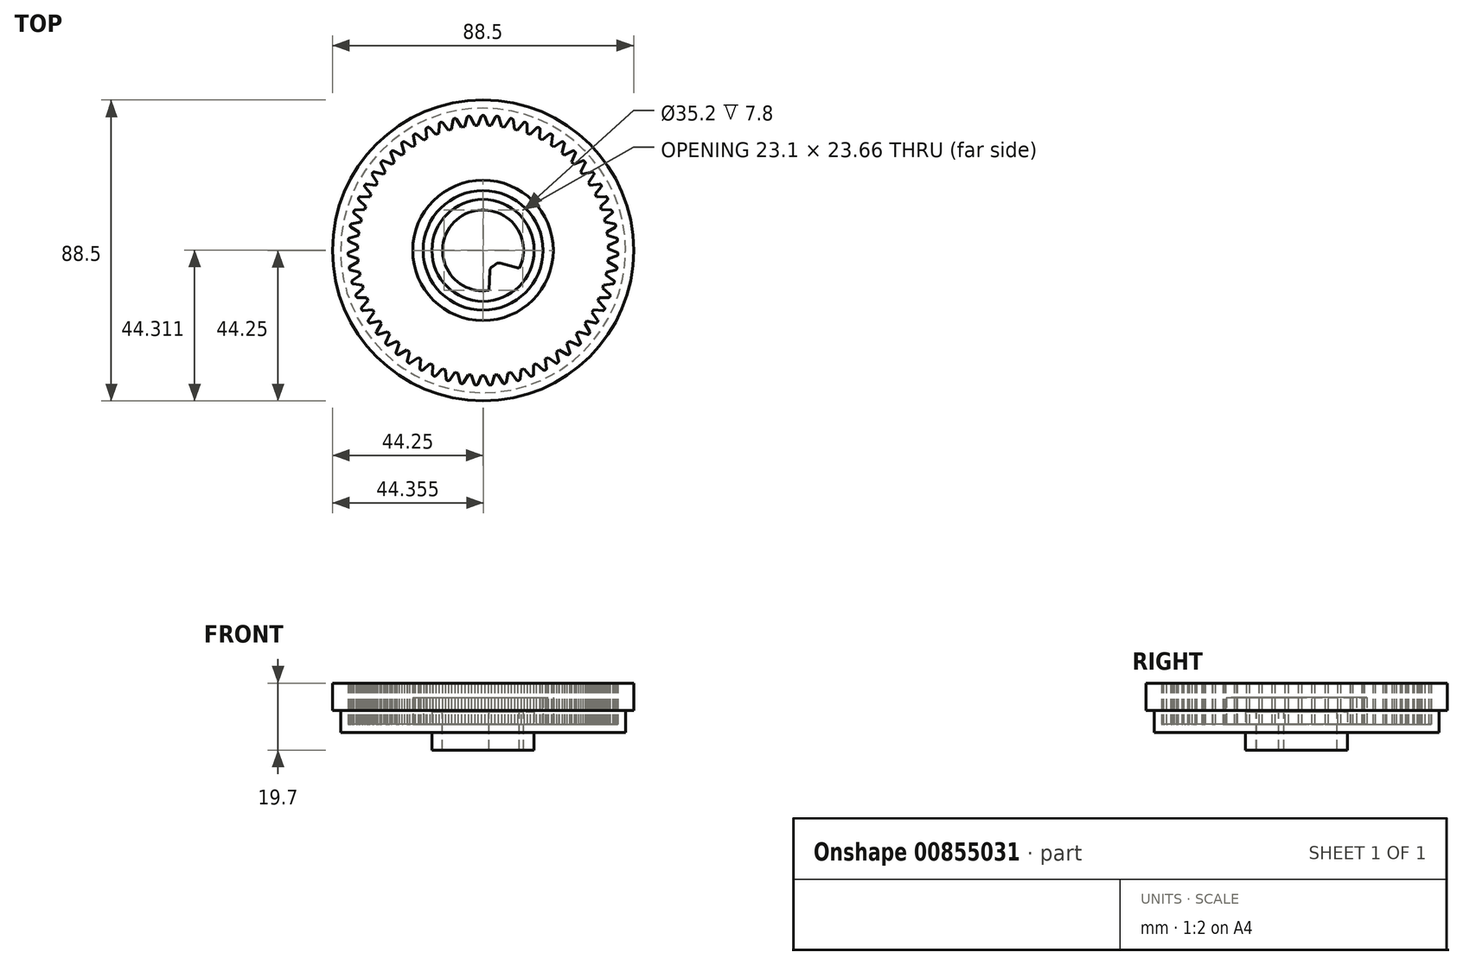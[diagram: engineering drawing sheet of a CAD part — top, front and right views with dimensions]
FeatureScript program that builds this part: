
annotation { "Feature Type Name" : "Feature", "Feature Type Description" : "" }
export const myFeature = defineFeature(function(context is Context, id is Id, definition is map)
    precondition{}
    {
        {
            var Q0;
            Q0=qCreatedBy(makeId("Front.planeOp"),FACE);
            var sketch = newSketch(context, id + "F0", { "sketchPlane" : qUnion([Q0])});
            skLineSegment(sketch, "E0", {"start": v(0, 3.6) * mm, "end": v(-15, 3.6) * mm});
            skLineSegment(sketch, "E1", {"start": v(-15, 3.6) * mm, "end": v(-15, 0) * mm});
            skLineSegment(sketch, "E2", {"start": v(-15, 0) * mm, "end": v(-17.6, 0) * mm});
            skLineSegment(sketch, "E3", {"start": v(-17.6, 0) * mm, "end": v(-17.6, 7.8) * mm});
            skLineSegment(sketch, "E4", {"start": v(-17.6, 7.8) * mm, "end": v(-20.65, 7.8) * mm});
            skLineSegment(sketch, "E5", {"start": v(-20.65, 7.8) * mm, "end": v(-20.65, 0) * mm});
            skLineSegment(sketch, "E6", {"start": v(-20.65, 0) * mm, "end": v(-39.65, 0) * mm});
            skLineSegment(sketch, "E7", {"start": v(-39.65, 0) * mm, "end": v(-39.65, 12.1) * mm});
            skLineSegment(sketch, "E8", {"start": v(-39.65, 12.1) * mm, "end": v(-44.25, 12.1) * mm});
            skLineSegment(sketch, "E9", {"start": v(-44.25, 12.1) * mm, "end": v(-44.25, 4.1) * mm});
            skLineSegment(sketch, "E10", {"start": v(-44.25, 4.1) * mm, "end": v(-41.85, 4.1) * mm});
            skLineSegment(sketch, "E11", {"start": v(-41.85, 4.1) * mm, "end": v(-41.85, -2.4) * mm});
            skLineSegment(sketch, "E12", {"start": v(-41.85, -2.4) * mm, "end": v(-15, -2.4) * mm});
            skLineSegment(sketch, "E13", {"start": v(-15, -2.4) * mm, "end": v(-15, -7.6) * mm});
            skLineSegment(sketch, "E14", {"start": v(-15, -7.6) * mm, "end": v(0, -7.6) * mm});
            skLineSegment(sketch, "E15", {"start": v(0, -7.6) * mm, "end": v(0, 3.6) * mm});
            skLineSegment(sketch, "E16", {"start": v(-9.3, 3.6) * mm, "end": v(-9.3, -7.6) * mm});
            skSolve(sketch);
        }
        {
            var Q0;
            {var subQ0=sQuery(id+"F0.wireOp",EDGE,"E1");Q0=makeQuery(id+"F0.imprint","IMPRINT",FACE,{"disambiguationData":[TD([[makeQuery(id+"F0.imprint","IMPRINT",EDGE,{"derivedFrom":subQ0}),1.0]])]});}
            var Q1;
            {var subQ0=sQuery(id+"F0.wireOp",EDGE,"E15");Q1=makeQuery(id+"F0.imprint","IMPRINT",FACE,{"disambiguationData":[TD([[makeQuery(id+"F0.imprint","IMPRINT",EDGE,{"derivedFrom":subQ0}),1.0]])]});}
            var Q2;
            Q2=sQuery(id+"F0.wireOp",EDGE,"E15");
            revolve(context, id + "F1", {"surfaceOperationType" : NewSurfaceOperationType.NEW, "entities" : qUnion([Q0, Q1]), "axis" : qUnion([Q2]), "revolveType" : RevolveType.FULL});
        }
        {
            var Q0;
            Q0=makeQuery(id+"F1.opRevolve","SWEPT_FACE",FACE,{"disambiguationData":[OSD([sQuery(id+"F0.wireOp",EDGE,"E6")])]});
            var sketch = newSketch(context, id + "F2", { "sketchPlane" : qUnion([Q0])});
            skLineSegment(sketch, "E17", {"start": v(0.04, -39.65) * mm, "end": v(0.04, -36.85) * mm});
            skLineSegment(sketch, "E18", {"start": v(0.04, -36.85) * mm, "end": v(-0.46, -36.85) * mm});
            skLineSegment(sketch, "E19", {"start": v(0.04, -39.65) * mm, "end": v(-1.96, -39.65) * mm});
            skLineSegment(sketch, "E20", {"start": v(-1.96, -39.65) * mm, "end": v(-1.96, -39.6) * mm});
            skArc(sketch, "E21", {"start": v(-1.96, -39.6) * mm, "mid": v(-1.73, -39.54) * mm, "end": v(-1.58, -39.36) * mm});
            skLineSegment(sketch, "E22", {"start": v(-0.46, -36.85) * mm, "end": v(-1.58, -39.36) * mm});
            skLineSegment(sketch, "E23.MirrorCS", {"start": v(-0.04, -36.85) * mm, "end": v(0.46, -36.85) * mm});
            skLineSegment(sketch, "E24.MirrorCS", {"start": v(0.46, -36.85) * mm, "end": v(1.58, -39.36) * mm});
            skArc(sketch, "E25.MirrorCS", {"start": v(1.96, -39.6) * mm, "mid": v(1.73, -39.54) * mm, "end": v(1.58, -39.36) * mm});
            skLineSegment(sketch, "E26.MirrorCS", {"start": v(-0.04, -39.65) * mm, "end": v(1.96, -39.65) * mm});
            skLineSegment(sketch, "E27.MirrorCS", {"start": v(1.96, -39.65) * mm, "end": v(1.96, -39.6) * mm});
            skLineSegment(sketch, "E28.1.0", {"start": v(3.45, -36.7) * mm, "end": v(2.62, -39.3) * mm});
            skLineSegment(sketch, "E28.1.1", {"start": v(3.95, -36.64) * mm, "end": v(3.45, -36.7) * mm});
            skLineSegment(sketch, "E28.1.2", {"start": v(3.88, -36.64) * mm, "end": v(4.38, -36.6) * mm});
            skLineSegment(sketch, "E28.1.3", {"start": v(4.38, -36.6) * mm, "end": v(5.75, -38.97) * mm});
            skArc(sketch, "E28.1.4", {"start": v(6.16, -39.17) * mm, "mid": v(5.93, -39.13) * mm, "end": v(5.75, -38.97) * mm});
            skLineSegment(sketch, "E28.1.5", {"start": v(6.17, -39.22) * mm, "end": v(6.16, -39.17) * mm});
            skLineSegment(sketch, "E28.1.6", {"start": v(4.18, -39.43) * mm, "end": v(6.17, -39.22) * mm});
            skLineSegment(sketch, "E28.1.7", {"start": v(4.25, -39.42) * mm, "end": v(2.26, -39.64) * mm});
            skLineSegment(sketch, "E28.1.8", {"start": v(2.26, -39.64) * mm, "end": v(2.26, -39.59) * mm});
            skArc(sketch, "E28.1.9", {"start": v(2.26, -39.59) * mm, "mid": v(2.48, -39.5) * mm, "end": v(2.62, -39.3) * mm});
            skLineSegment(sketch, "E28.2.0", {"start": v(7.34, -36.12) * mm, "end": v(6.78, -38.8) * mm});
            skLineSegment(sketch, "E28.2.1", {"start": v(7.82, -36) * mm, "end": v(7.34, -36.12) * mm});
            skLineSegment(sketch, "E28.2.2", {"start": v(7.76, -36.02) * mm, "end": v(8.24, -35.92) * mm});
            skLineSegment(sketch, "E28.2.3", {"start": v(8.24, -35.92) * mm, "end": v(9.86, -38.14) * mm});
            skArc(sketch, "E28.2.4", {"start": v(10.29, -38.3) * mm, "mid": v(10.05, -38.28) * mm, "end": v(9.86, -38.14) * mm});
            skLineSegment(sketch, "E28.2.5", {"start": v(10.3, -38.34) * mm, "end": v(10.29, -38.3) * mm});
            skLineSegment(sketch, "E28.2.6", {"start": v(8.34, -38.76) * mm, "end": v(10.3, -38.34) * mm});
            skLineSegment(sketch, "E28.2.7", {"start": v(8.42, -38.75) * mm, "end": v(6.46, -39.17) * mm});
            skLineSegment(sketch, "E28.2.8", {"start": v(6.46, -39.17) * mm, "end": v(6.45, -39.12) * mm});
            skArc(sketch, "E28.2.9", {"start": v(6.45, -39.12) * mm, "mid": v(6.67, -39.02) * mm, "end": v(6.78, -38.8) * mm});
            skLineSegment(sketch, "E28.3.0", {"start": v(11.13, -35.13) * mm, "end": v(10.87, -37.87) * mm});
            skLineSegment(sketch, "E28.3.1", {"start": v(11.6, -34.97) * mm, "end": v(11.13, -35.13) * mm});
            skLineSegment(sketch, "E28.3.2", {"start": v(11.54, -35) * mm, "end": v(12.02, -34.84) * mm});
            skLineSegment(sketch, "E28.3.3", {"start": v(12.02, -34.84) * mm, "end": v(13.86, -36.88) * mm});
            skArc(sketch, "E28.3.4", {"start": v(14.3, -36.98) * mm, "mid": v(14.06, -37) * mm, "end": v(13.86, -36.88) * mm});
            skLineSegment(sketch, "E28.3.5", {"start": v(14.32, -37.03) * mm, "end": v(14.3, -36.98) * mm});
            skLineSegment(sketch, "E28.3.6", {"start": v(12.42, -37.66) * mm, "end": v(14.32, -37.03) * mm});
            skLineSegment(sketch, "E28.3.7", {"start": v(12.49, -37.63) * mm, "end": v(10.6, -38.26) * mm});
            skLineSegment(sketch, "E28.3.8", {"start": v(10.6, -38.26) * mm, "end": v(10.57, -38.21) * mm});
            skArc(sketch, "E28.3.9", {"start": v(10.57, -38.21) * mm, "mid": v(10.77, -38.09) * mm, "end": v(10.87, -37.87) * mm});
            skLineSegment(sketch, "E28.4.0", {"start": v(14.8, -33.75) * mm, "end": v(14.83, -36.5) * mm});
            skLineSegment(sketch, "E28.4.1", {"start": v(15.26, -33.54) * mm, "end": v(14.8, -33.75) * mm});
            skLineSegment(sketch, "E28.4.2", {"start": v(15.2, -33.57) * mm, "end": v(15.65, -33.36) * mm});
            skLineSegment(sketch, "E28.4.3", {"start": v(15.65, -33.36) * mm, "end": v(17.7, -35.2) * mm});
            skArc(sketch, "E28.4.4", {"start": v(18.15, -35.25) * mm, "mid": v(17.92, -35.3) * mm, "end": v(17.7, -35.2) * mm});
            skLineSegment(sketch, "E28.4.5", {"start": v(18.17, -35.3) * mm, "end": v(18.15, -35.25) * mm});
            skLineSegment(sketch, "E28.4.6", {"start": v(16.35, -36.12) * mm, "end": v(18.17, -35.3) * mm});
            skLineSegment(sketch, "E28.4.7", {"start": v(16.42, -36.1) * mm, "end": v(14.6, -36.92) * mm});
            skLineSegment(sketch, "E28.4.8", {"start": v(14.6, -36.92) * mm, "end": v(14.58, -36.87) * mm});
            skArc(sketch, "E28.4.9", {"start": v(14.58, -36.87) * mm, "mid": v(14.76, -36.72) * mm, "end": v(14.83, -36.5) * mm});
            skLineSegment(sketch, "E28.5.0", {"start": v(18.3, -31.98) * mm, "end": v(18.63, -34.71) * mm});
            skLineSegment(sketch, "E28.5.1", {"start": v(18.74, -31.73) * mm, "end": v(18.3, -31.98) * mm});
            skLineSegment(sketch, "E28.5.2", {"start": v(18.68, -31.77) * mm, "end": v(19.1, -31.51) * mm});
            skLineSegment(sketch, "E28.5.3", {"start": v(19.1, -31.51) * mm, "end": v(21.34, -33.11) * mm});
            skArc(sketch, "E28.5.4", {"start": v(21.8, -33.12) * mm, "mid": v(21.57, -33.19) * mm, "end": v(21.34, -33.11) * mm});
            skLineSegment(sketch, "E28.5.5", {"start": v(21.82, -33.17) * mm, "end": v(21.8, -33.12) * mm});
            skLineSegment(sketch, "E28.5.6", {"start": v(20.1, -34.18) * mm, "end": v(21.82, -33.17) * mm});
            skLineSegment(sketch, "E28.5.7", {"start": v(20.16, -34.14) * mm, "end": v(18.44, -35.16) * mm});
            skLineSegment(sketch, "E28.5.8", {"start": v(18.44, -35.16) * mm, "end": v(18.41, -35.11) * mm});
            skArc(sketch, "E28.5.9", {"start": v(18.41, -35.11) * mm, "mid": v(18.58, -34.95) * mm, "end": v(18.63, -34.71) * mm});
            skLineSegment(sketch, "E28.6.0", {"start": v(21.6, -29.86) * mm, "end": v(22.2, -32.54) * mm});
            skLineSegment(sketch, "E28.6.1", {"start": v(22, -29.56) * mm, "end": v(21.6, -29.86) * mm});
            skLineSegment(sketch, "E28.6.2", {"start": v(21.95, -29.6) * mm, "end": v(22.35, -29.3) * mm});
            skLineSegment(sketch, "E28.6.3", {"start": v(22.35, -29.3) * mm, "end": v(24.74, -30.66) * mm});
            skArc(sketch, "E28.6.4", {"start": v(25.2, -30.62) * mm, "mid": v(24.97, -30.7) * mm, "end": v(24.74, -30.66) * mm});
            skLineSegment(sketch, "E28.6.5", {"start": v(25.22, -30.66) * mm, "end": v(25.2, -30.62) * mm});
            skLineSegment(sketch, "E28.6.6", {"start": v(23.62, -31.85) * mm, "end": v(25.22, -30.66) * mm});
            skLineSegment(sketch, "E28.6.7", {"start": v(23.68, -31.8) * mm, "end": v(22.07, -33) * mm});
            skLineSegment(sketch, "E28.6.8", {"start": v(22.07, -33) * mm, "end": v(22.04, -32.96) * mm});
            skArc(sketch, "E28.6.9", {"start": v(22.04, -32.96) * mm, "mid": v(22.2, -32.77) * mm, "end": v(22.2, -32.54) * mm});
            skLineSegment(sketch, "E28.7.0", {"start": v(24.65, -27.4) * mm, "end": v(25.54, -30) * mm});
            skLineSegment(sketch, "E28.7.1", {"start": v(25.02, -27.05) * mm, "end": v(24.65, -27.4) * mm});
            skLineSegment(sketch, "E28.7.2", {"start": v(24.97, -27.1) * mm, "end": v(25.34, -26.76) * mm});
            skLineSegment(sketch, "E28.7.3", {"start": v(25.34, -26.76) * mm, "end": v(27.86, -27.85) * mm});
            skArc(sketch, "E28.7.4", {"start": v(28.3, -27.77) * mm, "mid": v(28.1, -27.88) * mm, "end": v(27.86, -27.85) * mm});
            skLineSegment(sketch, "E28.7.5", {"start": v(28.34, -27.8) * mm, "end": v(28.3, -27.77) * mm});
            skLineSegment(sketch, "E28.7.6", {"start": v(26.87, -29.16) * mm, "end": v(28.34, -27.8) * mm});
            skLineSegment(sketch, "E28.7.7", {"start": v(26.92, -29.1) * mm, "end": v(25.45, -30.47) * mm});
            skLineSegment(sketch, "E28.7.8", {"start": v(25.45, -30.47) * mm, "end": v(25.42, -30.43) * mm});
            skArc(sketch, "E28.7.9", {"start": v(25.42, -30.43) * mm, "mid": v(25.55, -30.23) * mm, "end": v(25.54, -30) * mm});
            skLineSegment(sketch, "E28.8.0", {"start": v(27.43, -24.62) * mm, "end": v(28.59, -27.1) * mm});
            skLineSegment(sketch, "E28.8.1", {"start": v(27.76, -24.24) * mm, "end": v(27.43, -24.62) * mm});
            skLineSegment(sketch, "E28.8.2", {"start": v(27.7, -24.3) * mm, "end": v(28.04, -23.92) * mm});
            skLineSegment(sketch, "E28.8.3", {"start": v(28.04, -23.92) * mm, "end": v(30.66, -24.73) * mm});
            skArc(sketch, "E28.8.4", {"start": v(31.1, -24.6) * mm, "mid": v(30.9, -24.74) * mm, "end": v(30.66, -24.73) * mm});
            skLineSegment(sketch, "E28.8.5", {"start": v(31.13, -24.63) * mm, "end": v(31.1, -24.6) * mm});
            skLineSegment(sketch, "E28.8.6", {"start": v(29.81, -26.14) * mm, "end": v(31.13, -24.63) * mm});
            skLineSegment(sketch, "E28.8.7", {"start": v(29.86, -26.08) * mm, "end": v(28.55, -27.59) * mm});
            skLineSegment(sketch, "E28.8.8", {"start": v(28.55, -27.59) * mm, "end": v(28.51, -27.55) * mm});
            skArc(sketch, "E28.8.9", {"start": v(28.51, -27.55) * mm, "mid": v(28.62, -27.34) * mm, "end": v(28.59, -27.1) * mm});
            skLineSegment(sketch, "E28.9.0", {"start": v(29.89, -21.56) * mm, "end": v(31.3, -23.92) * mm});
            skLineSegment(sketch, "E28.9.1", {"start": v(30.17, -21.15) * mm, "end": v(29.89, -21.56) * mm});
            skLineSegment(sketch, "E28.9.2", {"start": v(30.13, -21.2) * mm, "end": v(30.42, -20.8) * mm});
            skLineSegment(sketch, "E28.9.3", {"start": v(30.42, -20.8) * mm, "end": v(33.12, -21.34) * mm});
            skArc(sketch, "E28.9.4", {"start": v(33.53, -21.16) * mm, "mid": v(33.35, -21.31) * mm, "end": v(33.12, -21.34) * mm});
            skLineSegment(sketch, "E28.9.5", {"start": v(33.58, -21.19) * mm, "end": v(33.53, -21.16) * mm});
            skLineSegment(sketch, "E28.9.6", {"start": v(32.42, -22.82) * mm, "end": v(33.58, -21.19) * mm});
            skLineSegment(sketch, "E28.9.7", {"start": v(32.47, -22.76) * mm, "end": v(31.32, -24.4) * mm});
            skLineSegment(sketch, "E28.9.8", {"start": v(31.32, -24.4) * mm, "end": v(31.28, -24.37) * mm});
            skArc(sketch, "E28.9.9", {"start": v(31.28, -24.37) * mm, "mid": v(31.36, -24.15) * mm, "end": v(31.3, -23.92) * mm});
            skLineSegment(sketch, "E28.10.0", {"start": v(32, -18.26) * mm, "end": v(33.67, -20.45) * mm});
            skLineSegment(sketch, "E28.10.1", {"start": v(32.25, -17.82) * mm, "end": v(32, -18.26) * mm});
            skLineSegment(sketch, "E28.10.2", {"start": v(32.22, -17.89) * mm, "end": v(32.46, -17.45) * mm});
            skLineSegment(sketch, "E28.10.3", {"start": v(32.46, -17.45) * mm, "end": v(35.2, -17.7) * mm});
            skArc(sketch, "E28.10.4", {"start": v(35.6, -17.47) * mm, "mid": v(35.43, -17.64) * mm, "end": v(35.2, -17.7) * mm});
            skLineSegment(sketch, "E28.10.5", {"start": v(35.64, -17.5) * mm, "end": v(35.6, -17.47) * mm});
            skLineSegment(sketch, "E28.10.6", {"start": v(34.67, -19.25) * mm, "end": v(35.64, -17.5) * mm});
            skLineSegment(sketch, "E28.10.7", {"start": v(34.7, -19.18) * mm, "end": v(33.74, -20.93) * mm});
            skLineSegment(sketch, "E28.10.8", {"start": v(33.74, -20.93) * mm, "end": v(33.7, -20.9) * mm});
            skArc(sketch, "E28.10.9", {"start": v(33.7, -20.9) * mm, "mid": v(33.75, -20.68) * mm, "end": v(33.67, -20.45) * mm});
            skLineSegment(sketch, "E28.11.0", {"start": v(33.77, -14.76) * mm, "end": v(35.65, -16.76) * mm});
            skLineSegment(sketch, "E28.11.1", {"start": v(33.96, -14.3) * mm, "end": v(33.77, -14.76) * mm});
            skLineSegment(sketch, "E28.11.2", {"start": v(33.94, -14.36) * mm, "end": v(34.13, -13.9) * mm});
            skLineSegment(sketch, "E28.11.3", {"start": v(34.13, -13.9) * mm, "end": v(36.88, -13.85) * mm});
            skArc(sketch, "E28.11.4", {"start": v(37.25, -13.6) * mm, "mid": v(37.1, -13.78) * mm, "end": v(36.88, -13.85) * mm});
            skLineSegment(sketch, "E28.11.5", {"start": v(37.3, -13.6) * mm, "end": v(37.25, -13.6) * mm});
            skLineSegment(sketch, "E28.11.6", {"start": v(36.52, -15.45) * mm, "end": v(37.3, -13.6) * mm});
            skLineSegment(sketch, "E28.11.7", {"start": v(36.54, -15.38) * mm, "end": v(35.77, -17.23) * mm});
            skLineSegment(sketch, "E28.11.8", {"start": v(35.77, -17.23) * mm, "end": v(35.72, -17.2) * mm});
            skArc(sketch, "E28.11.9", {"start": v(35.72, -17.2) * mm, "mid": v(35.76, -16.97) * mm, "end": v(35.65, -16.76) * mm});
            skLineSegment(sketch, "E28.12.0", {"start": v(35.15, -11.08) * mm, "end": v(37.23, -12.87) * mm});
            skLineSegment(sketch, "E28.12.1", {"start": v(35.3, -10.6) * mm, "end": v(35.15, -11.08) * mm});
            skLineSegment(sketch, "E28.12.2", {"start": v(35.27, -10.67) * mm, "end": v(35.42, -10.2) * mm});
            skLineSegment(sketch, "E28.12.3", {"start": v(35.42, -10.2) * mm, "end": v(38.14, -9.85) * mm});
            skArc(sketch, "E28.12.4", {"start": v(38.48, -9.55) * mm, "mid": v(38.36, -9.76) * mm, "end": v(38.14, -9.85) * mm});
            skLineSegment(sketch, "E28.12.5", {"start": v(38.53, -9.57) * mm, "end": v(38.48, -9.55) * mm});
            skLineSegment(sketch, "E28.12.6", {"start": v(37.95, -11.48) * mm, "end": v(38.53, -9.57) * mm});
            skLineSegment(sketch, "E28.12.7", {"start": v(37.97, -11.41) * mm, "end": v(37.4, -13.33) * mm});
            skLineSegment(sketch, "E28.12.8", {"start": v(37.4, -13.33) * mm, "end": v(37.35, -13.31) * mm});
            skArc(sketch, "E28.12.9", {"start": v(37.35, -13.31) * mm, "mid": v(37.36, -13.07) * mm, "end": v(37.23, -12.87) * mm});
            skLineSegment(sketch, "E28.13.0", {"start": v(36.13, -7.28) * mm, "end": v(38.39, -8.84) * mm});
            skLineSegment(sketch, "E28.13.1", {"start": v(36.22, -6.8) * mm, "end": v(36.13, -7.28) * mm});
            skLineSegment(sketch, "E28.13.2", {"start": v(36.2, -6.86) * mm, "end": v(36.3, -6.37) * mm});
            skLineSegment(sketch, "E28.13.3", {"start": v(36.3, -6.37) * mm, "end": v(38.97, -5.74) * mm});
            skArc(sketch, "E28.13.4", {"start": v(39.28, -5.4) * mm, "mid": v(39.18, -5.62) * mm, "end": v(38.97, -5.74) * mm});
            skLineSegment(sketch, "E28.13.5", {"start": v(39.33, -5.42) * mm, "end": v(39.28, -5.4) * mm});
            skLineSegment(sketch, "E28.13.6", {"start": v(38.96, -7.38) * mm, "end": v(39.33, -5.42) * mm});
            skLineSegment(sketch, "E28.13.7", {"start": v(38.97, -7.3) * mm, "end": v(38.6, -9.28) * mm});
            skLineSegment(sketch, "E28.13.8", {"start": v(38.6, -9.28) * mm, "end": v(38.55, -9.27) * mm});
            skArc(sketch, "E28.13.9", {"start": v(38.55, -9.27) * mm, "mid": v(38.54, -9.03) * mm, "end": v(38.39, -8.84) * mm});
            skLineSegment(sketch, "E28.14.0", {"start": v(36.7, -3.4) * mm, "end": v(39.11, -4.71) * mm});
            skLineSegment(sketch, "E28.14.1", {"start": v(36.74, -2.9) * mm, "end": v(36.7, -3.4) * mm});
            skLineSegment(sketch, "E28.14.2", {"start": v(36.73, -2.98) * mm, "end": v(36.77, -2.48) * mm});
            skLineSegment(sketch, "E28.14.3", {"start": v(36.77, -2.48) * mm, "end": v(39.36, -1.57) * mm});
            skArc(sketch, "E28.14.4", {"start": v(39.63, -1.2) * mm, "mid": v(39.55, -1.43) * mm, "end": v(39.36, -1.57) * mm});
            skLineSegment(sketch, "E28.14.5", {"start": v(39.68, -1.2) * mm, "end": v(39.63, -1.2) * mm});
            skLineSegment(sketch, "E28.14.6", {"start": v(39.52, -3.2) * mm, "end": v(39.68, -1.2) * mm});
            skLineSegment(sketch, "E28.14.7", {"start": v(39.53, -3.13) * mm, "end": v(39.37, -5.12) * mm});
            skLineSegment(sketch, "E28.14.8", {"start": v(39.37, -5.12) * mm, "end": v(39.32, -5.12) * mm});
            skArc(sketch, "E28.14.9", {"start": v(39.32, -5.12) * mm, "mid": v(39.28, -4.88) * mm, "end": v(39.11, -4.71) * mm});
            skLineSegment(sketch, "E28.15.0", {"start": v(36.85, 0.52) * mm, "end": v(39.4, -0.53) * mm});
            skLineSegment(sketch, "E28.15.1", {"start": v(36.84, 1.02) * mm, "end": v(36.85, 0.52) * mm});
            skLineSegment(sketch, "E28.15.2", {"start": v(36.84, 0.95) * mm, "end": v(36.82, 1.45) * mm});
            skLineSegment(sketch, "E28.15.3", {"start": v(36.82, 1.45) * mm, "end": v(39.3, 2.62) * mm});
            skArc(sketch, "E28.15.4", {"start": v(39.54, 3.02) * mm, "mid": v(39.48, 2.78) * mm, "end": v(39.3, 2.62) * mm});
            skLineSegment(sketch, "E28.15.5", {"start": v(39.59, 3.02) * mm, "end": v(39.54, 3.02) * mm});
            skLineSegment(sketch, "E28.15.6", {"start": v(39.64, 1.02) * mm, "end": v(39.59, 3.02) * mm});
            skLineSegment(sketch, "E28.15.7", {"start": v(39.63, 1.1) * mm, "end": v(39.7, -0.9) * mm});
            skLineSegment(sketch, "E28.15.8", {"start": v(39.7, -0.9) * mm, "end": v(39.64, -0.9) * mm});
            skArc(sketch, "E28.15.9", {"start": v(39.64, -0.9) * mm, "mid": v(39.57, -0.68) * mm, "end": v(39.4, -0.53) * mm});
            skLineSegment(sketch, "E28.16.0", {"start": v(36.59, 4.43) * mm, "end": v(39.22, 3.66) * mm});
            skLineSegment(sketch, "E28.16.1", {"start": v(36.52, 4.93) * mm, "end": v(36.59, 4.43) * mm});
            skLineSegment(sketch, "E28.16.2", {"start": v(36.53, 4.86) * mm, "end": v(36.46, 5.35) * mm});
            skLineSegment(sketch, "E28.16.3", {"start": v(36.46, 5.35) * mm, "end": v(38.8, 6.79) * mm});
            skArc(sketch, "E28.16.4", {"start": v(39, 7.2) * mm, "mid": v(38.96, 6.97) * mm, "end": v(38.8, 6.79) * mm});
            skLineSegment(sketch, "E28.16.5", {"start": v(39.04, 7.2) * mm, "end": v(39, 7.2) * mm});
            skLineSegment(sketch, "E28.16.6", {"start": v(39.3, 5.23) * mm, "end": v(39.04, 7.2) * mm});
            skLineSegment(sketch, "E28.16.7", {"start": v(39.3, 5.3) * mm, "end": v(39.56, 3.32) * mm});
            skLineSegment(sketch, "E28.16.8", {"start": v(39.56, 3.32) * mm, "end": v(39.51, 3.31) * mm});
            skArc(sketch, "E28.16.9", {"start": v(39.51, 3.31) * mm, "mid": v(39.42, 3.53) * mm, "end": v(39.22, 3.66) * mm});
            skLineSegment(sketch, "E28.17.0", {"start": v(35.9, 8.3) * mm, "end": v(38.61, 7.81) * mm});
            skLineSegment(sketch, "E28.17.1", {"start": v(35.79, 8.78) * mm, "end": v(35.9, 8.3) * mm});
            skLineSegment(sketch, "E28.17.2", {"start": v(35.8, 8.71) * mm, "end": v(35.69, 9.2) * mm});
            skLineSegment(sketch, "E28.17.3", {"start": v(35.69, 9.2) * mm, "end": v(37.86, 10.87) * mm});
            skArc(sketch, "E28.17.4", {"start": v(38, 11.3) * mm, "mid": v(38, 11.07) * mm, "end": v(37.86, 10.87) * mm});
            skLineSegment(sketch, "E28.17.5", {"start": v(38.05, 11.32) * mm, "end": v(38, 11.3) * mm});
            skLineSegment(sketch, "E28.17.6", {"start": v(38.53, 9.37) * mm, "end": v(38.05, 11.32) * mm});
            skLineSegment(sketch, "E28.17.7", {"start": v(38.5, 9.45) * mm, "end": v(38.98, 7.5) * mm});
            skLineSegment(sketch, "E28.17.8", {"start": v(38.98, 7.5) * mm, "end": v(38.94, 7.5) * mm});
            skArc(sketch, "E28.17.9", {"start": v(38.94, 7.5) * mm, "mid": v(38.82, 7.7) * mm, "end": v(38.61, 7.81) * mm});
            skLineSegment(sketch, "E28.18.0", {"start": v(34.82, 12.06) * mm, "end": v(37.56, 11.87) * mm});
            skLineSegment(sketch, "E28.18.1", {"start": v(34.65, 12.53) * mm, "end": v(34.82, 12.06) * mm});
            skLineSegment(sketch, "E28.18.2", {"start": v(34.68, 12.47) * mm, "end": v(34.5, 12.94) * mm});
            skLineSegment(sketch, "E28.18.3", {"start": v(34.5, 12.94) * mm, "end": v(36.5, 14.84) * mm});
            skArc(sketch, "E28.18.4", {"start": v(36.59, 15.28) * mm, "mid": v(36.6, 15.04) * mm, "end": v(36.5, 14.84) * mm});
            skLineSegment(sketch, "E28.18.5", {"start": v(36.63, 15.3) * mm, "end": v(36.59, 15.28) * mm});
            skLineSegment(sketch, "E28.18.6", {"start": v(37.31, 13.42) * mm, "end": v(36.63, 15.3) * mm});
            skLineSegment(sketch, "E28.18.7", {"start": v(37.29, 13.49) * mm, "end": v(37.97, 11.6) * mm});
            skLineSegment(sketch, "E28.18.8", {"start": v(37.97, 11.6) * mm, "end": v(37.92, 11.59) * mm});
            skArc(sketch, "E28.18.9", {"start": v(37.92, 11.59) * mm, "mid": v(37.79, 11.78) * mm, "end": v(37.56, 11.87) * mm});
            skLineSegment(sketch, "E28.19.0", {"start": v(33.34, 15.7) * mm, "end": v(36.09, 15.8) * mm});
            skLineSegment(sketch, "E28.19.1", {"start": v(33.12, 16.15) * mm, "end": v(33.34, 15.7) * mm});
            skLineSegment(sketch, "E28.19.2", {"start": v(33.16, 16.08) * mm, "end": v(32.94, 16.53) * mm});
            skLineSegment(sketch, "E28.19.3", {"start": v(32.94, 16.53) * mm, "end": v(34.71, 18.63) * mm});
            skArc(sketch, "E28.19.4", {"start": v(34.76, 19.08) * mm, "mid": v(34.8, 18.85) * mm, "end": v(34.71, 18.63) * mm});
            skLineSegment(sketch, "E28.19.5", {"start": v(34.8, 19.1) * mm, "end": v(34.76, 19.08) * mm});
            skLineSegment(sketch, "E28.19.6", {"start": v(35.67, 17.3) * mm, "end": v(34.8, 19.1) * mm});
            skLineSegment(sketch, "E28.19.7", {"start": v(35.64, 17.37) * mm, "end": v(36.52, 15.58) * mm});
            skLineSegment(sketch, "E28.19.8", {"start": v(36.52, 15.58) * mm, "end": v(36.47, 15.55) * mm});
            skArc(sketch, "E28.19.9", {"start": v(36.47, 15.55) * mm, "mid": v(36.32, 15.73) * mm, "end": v(36.09, 15.8) * mm});
            skLineSegment(sketch, "E28.20.0", {"start": v(31.49, 19.15) * mm, "end": v(34.2, 19.54) * mm});
            skLineSegment(sketch, "E28.20.1", {"start": v(31.22, 19.58) * mm, "end": v(31.49, 19.15) * mm});
            skLineSegment(sketch, "E28.20.2", {"start": v(31.26, 19.52) * mm, "end": v(31, 19.94) * mm});
            skLineSegment(sketch, "E28.20.3", {"start": v(31, 19.94) * mm, "end": v(32.53, 22.22) * mm});
            skArc(sketch, "E28.20.4", {"start": v(32.53, 22.67) * mm, "mid": v(32.6, 22.44) * mm, "end": v(32.53, 22.22) * mm});
            skLineSegment(sketch, "E28.20.5", {"start": v(32.57, 22.7) * mm, "end": v(32.53, 22.67) * mm});
            skLineSegment(sketch, "E28.20.6", {"start": v(33.63, 21) * mm, "end": v(32.57, 22.7) * mm});
            skLineSegment(sketch, "E28.20.7", {"start": v(33.6, 21.06) * mm, "end": v(34.66, 19.37) * mm});
            skLineSegment(sketch, "E28.20.8", {"start": v(34.66, 19.37) * mm, "end": v(34.61, 19.34) * mm});
            skArc(sketch, "E28.20.9", {"start": v(34.61, 19.34) * mm, "mid": v(34.44, 19.5) * mm, "end": v(34.2, 19.54) * mm});
            skLineSegment(sketch, "E28.21.0", {"start": v(29.27, 22.4) * mm, "end": v(31.94, 23.07) * mm});
            skLineSegment(sketch, "E28.21.1", {"start": v(28.96, 22.78) * mm, "end": v(29.27, 22.4) * mm});
            skLineSegment(sketch, "E28.21.2", {"start": v(29, 22.73) * mm, "end": v(28.7, 23.12) * mm});
            skLineSegment(sketch, "E28.21.3", {"start": v(28.7, 23.12) * mm, "end": v(29.99, 25.55) * mm});
            skArc(sketch, "E28.21.4", {"start": v(29.94, 26) * mm, "mid": v(30.03, 25.78) * mm, "end": v(29.99, 25.55) * mm});
            skLineSegment(sketch, "E28.21.5", {"start": v(29.98, 26.03) * mm, "end": v(29.94, 26) * mm});
            skLineSegment(sketch, "E28.21.6", {"start": v(31.21, 24.46) * mm, "end": v(29.98, 26.03) * mm});
            skLineSegment(sketch, "E28.21.7", {"start": v(31.16, 24.51) * mm, "end": v(32.4, 22.94) * mm});
            skLineSegment(sketch, "E28.21.8", {"start": v(32.4, 22.94) * mm, "end": v(32.36, 22.91) * mm});
            skArc(sketch, "E28.21.9", {"start": v(32.36, 22.91) * mm, "mid": v(32.17, 23.06) * mm, "end": v(31.94, 23.07) * mm});
            skLineSegment(sketch, "E28.22.0", {"start": v(26.73, 25.37) * mm, "end": v(29.3, 26.33) * mm});
            skLineSegment(sketch, "E28.22.1", {"start": v(26.38, 25.73) * mm, "end": v(26.73, 25.37) * mm});
            skLineSegment(sketch, "E28.22.2", {"start": v(26.43, 25.68) * mm, "end": v(26.08, 26.04) * mm});
            skLineSegment(sketch, "E28.22.3", {"start": v(26.08, 26.04) * mm, "end": v(27.1, 28.6) * mm});
            skArc(sketch, "E28.22.4", {"start": v(27, 29.03) * mm, "mid": v(27.12, 28.83) * mm, "end": v(27.1, 28.6) * mm});
            skLineSegment(sketch, "E28.22.5", {"start": v(27.04, 29.07) * mm, "end": v(27, 29.03) * mm});
            skLineSegment(sketch, "E28.22.6", {"start": v(28.43, 27.63) * mm, "end": v(27.04, 29.07) * mm});
            skLineSegment(sketch, "E28.22.7", {"start": v(28.38, 27.69) * mm, "end": v(29.78, 26.26) * mm});
            skLineSegment(sketch, "E28.22.8", {"start": v(29.78, 26.26) * mm, "end": v(29.74, 26.22) * mm});
            skArc(sketch, "E28.22.9", {"start": v(29.74, 26.22) * mm, "mid": v(29.54, 26.34) * mm, "end": v(29.3, 26.33) * mm});
            skLineSegment(sketch, "E28.23.0", {"start": v(23.88, 28.07) * mm, "end": v(26.34, 29.3) * mm});
            skLineSegment(sketch, "E28.23.1", {"start": v(23.5, 28.4) * mm, "end": v(23.88, 28.07) * mm});
            skLineSegment(sketch, "E28.23.2", {"start": v(23.55, 28.35) * mm, "end": v(23.16, 28.67) * mm});
            skLineSegment(sketch, "E28.23.3", {"start": v(23.16, 28.67) * mm, "end": v(23.9, 31.3) * mm});
            skArc(sketch, "E28.23.4", {"start": v(23.76, 31.74) * mm, "mid": v(23.9, 31.55) * mm, "end": v(23.9, 31.3) * mm});
            skLineSegment(sketch, "E28.23.5", {"start": v(23.8, 31.78) * mm, "end": v(23.76, 31.74) * mm});
            skLineSegment(sketch, "E28.23.6", {"start": v(25.34, 30.5) * mm, "end": v(23.8, 31.78) * mm});
            skLineSegment(sketch, "E28.23.7", {"start": v(25.28, 30.55) * mm, "end": v(26.82, 29.27) * mm});
            skLineSegment(sketch, "E28.23.8", {"start": v(26.82, 29.27) * mm, "end": v(26.79, 29.23) * mm});
            skArc(sketch, "E28.23.9", {"start": v(26.79, 29.23) * mm, "mid": v(26.57, 29.34) * mm, "end": v(26.34, 29.3) * mm});
            skLineSegment(sketch, "E28.24.0", {"start": v(20.76, 30.45) * mm, "end": v(23.07, 31.93) * mm});
            skLineSegment(sketch, "E28.24.1", {"start": v(20.34, 30.73) * mm, "end": v(20.76, 30.45) * mm});
            skLineSegment(sketch, "E28.24.2", {"start": v(20.4, 30.69) * mm, "end": v(19.98, 30.96) * mm});
            skLineSegment(sketch, "E28.24.3", {"start": v(19.98, 30.96) * mm, "end": v(20.45, 33.67) * mm});
            skArc(sketch, "E28.24.4", {"start": v(20.26, 34.09) * mm, "mid": v(20.42, 33.9) * mm, "end": v(20.45, 33.67) * mm});
            skLineSegment(sketch, "E28.24.5", {"start": v(20.28, 34.13) * mm, "end": v(20.26, 34.09) * mm});
            skLineSegment(sketch, "E28.24.6", {"start": v(21.95, 33.02) * mm, "end": v(20.28, 34.13) * mm});
            skLineSegment(sketch, "E28.24.7", {"start": v(21.89, 33.06) * mm, "end": v(23.55, 31.96) * mm});
            skLineSegment(sketch, "E28.24.8", {"start": v(23.55, 31.96) * mm, "end": v(23.53, 31.92) * mm});
            skArc(sketch, "E28.24.9", {"start": v(23.53, 31.92) * mm, "mid": v(23.3, 32) * mm, "end": v(23.07, 31.93) * mm});
            skLineSegment(sketch, "E28.25.0", {"start": v(17.4, 32.48) * mm, "end": v(19.55, 34.2) * mm});
            skLineSegment(sketch, "E28.25.1", {"start": v(16.96, 32.72) * mm, "end": v(17.4, 32.48) * mm});
            skLineSegment(sketch, "E28.25.2", {"start": v(17.02, 32.68) * mm, "end": v(16.58, 32.91) * mm});
            skLineSegment(sketch, "E28.25.3", {"start": v(16.58, 32.91) * mm, "end": v(16.75, 35.66) * mm});
            skArc(sketch, "E28.25.4", {"start": v(16.52, 36.05) * mm, "mid": v(16.7, 35.89) * mm, "end": v(16.75, 35.66) * mm});
            skLineSegment(sketch, "E28.25.5", {"start": v(16.54, 36.09) * mm, "end": v(16.52, 36.05) * mm});
            skLineSegment(sketch, "E28.25.6", {"start": v(18.32, 35.17) * mm, "end": v(16.54, 36.09) * mm});
            skLineSegment(sketch, "E28.25.7", {"start": v(18.25, 35.2) * mm, "end": v(20.02, 34.28) * mm});
            skLineSegment(sketch, "E28.25.8", {"start": v(20.02, 34.28) * mm, "end": v(20, 34.24) * mm});
            skArc(sketch, "E28.25.9", {"start": v(20, 34.24) * mm, "mid": v(19.77, 34.29) * mm, "end": v(19.55, 34.2) * mm});
            skLineSegment(sketch, "E28.26.0", {"start": v(13.85, 34.15) * mm, "end": v(15.8, 36.09) * mm});
            skLineSegment(sketch, "E28.26.1", {"start": v(13.39, 34.33) * mm, "end": v(13.85, 34.15) * mm});
            skLineSegment(sketch, "E28.26.2", {"start": v(13.45, 34.3) * mm, "end": v(12.99, 34.49) * mm});
            skLineSegment(sketch, "E28.26.3", {"start": v(12.99, 34.49) * mm, "end": v(12.87, 37.24) * mm});
            skArc(sketch, "E28.26.4", {"start": v(12.6, 37.6) * mm, "mid": v(12.79, 37.46) * mm, "end": v(12.87, 37.24) * mm});
            skLineSegment(sketch, "E28.26.5", {"start": v(12.61, 37.64) * mm, "end": v(12.6, 37.6) * mm});
            skLineSegment(sketch, "E28.26.6", {"start": v(14.47, 36.91) * mm, "end": v(12.61, 37.64) * mm});
            skLineSegment(sketch, "E28.26.7", {"start": v(14.4, 36.94) * mm, "end": v(16.27, 36.21) * mm});
            skLineSegment(sketch, "E28.26.8", {"start": v(16.27, 36.21) * mm, "end": v(16.25, 36.17) * mm});
            skArc(sketch, "E28.26.9", {"start": v(16.25, 36.17) * mm, "mid": v(16.01, 36.2) * mm, "end": v(15.8, 36.09) * mm});
            skLineSegment(sketch, "E28.27.0", {"start": v(10.14, 35.43) * mm, "end": v(11.88, 37.56) * mm});
            skLineSegment(sketch, "E28.27.1", {"start": v(9.66, 35.56) * mm, "end": v(10.14, 35.43) * mm});
            skLineSegment(sketch, "E28.27.2", {"start": v(9.73, 35.54) * mm, "end": v(9.25, 35.67) * mm});
            skLineSegment(sketch, "E28.27.3", {"start": v(9.25, 35.67) * mm, "end": v(8.84, 38.4) * mm});
            skArc(sketch, "E28.27.4", {"start": v(8.53, 38.72) * mm, "mid": v(8.73, 38.6) * mm, "end": v(8.84, 38.4) * mm});
            skLineSegment(sketch, "E28.27.5", {"start": v(8.54, 38.77) * mm, "end": v(8.53, 38.72) * mm});
            skLineSegment(sketch, "E28.27.6", {"start": v(10.47, 38.24) * mm, "end": v(8.54, 38.77) * mm});
            skLineSegment(sketch, "E28.27.7", {"start": v(10.4, 38.26) * mm, "end": v(12.33, 37.74) * mm});
            skLineSegment(sketch, "E28.27.8", {"start": v(12.33, 37.74) * mm, "end": v(12.31, 37.69) * mm});
            skArc(sketch, "E28.27.9", {"start": v(12.31, 37.69) * mm, "mid": v(12.08, 37.7) * mm, "end": v(11.88, 37.56) * mm});
            skLineSegment(sketch, "E28.28.0", {"start": v(6.32, 36.3) * mm, "end": v(7.82, 38.61) * mm});
            skLineSegment(sketch, "E28.28.1", {"start": v(5.83, 36.39) * mm, "end": v(6.32, 36.3) * mm});
            skLineSegment(sketch, "E28.28.2", {"start": v(5.9, 36.38) * mm, "end": v(5.4, 36.45) * mm});
            skLineSegment(sketch, "E28.28.3", {"start": v(5.4, 36.45) * mm, "end": v(4.7, 39.11) * mm});
            skArc(sketch, "E28.28.4", {"start": v(4.36, 39.4) * mm, "mid": v(4.58, 39.31) * mm, "end": v(4.7, 39.11) * mm});
            skLineSegment(sketch, "E28.28.5", {"start": v(4.37, 39.46) * mm, "end": v(4.36, 39.4) * mm});
            skLineSegment(sketch, "E28.28.6", {"start": v(6.34, 39.14) * mm, "end": v(4.37, 39.46) * mm});
            skLineSegment(sketch, "E28.28.7", {"start": v(6.27, 39.15) * mm, "end": v(8.24, 38.83) * mm});
            skLineSegment(sketch, "E28.28.8", {"start": v(8.24, 38.83) * mm, "end": v(8.24, 38.79) * mm});
            skArc(sketch, "E28.28.9", {"start": v(8.24, 38.79) * mm, "mid": v(8, 38.76) * mm, "end": v(7.82, 38.61) * mm});
            skLineSegment(sketch, "E28.29.0", {"start": v(2.43, 36.77) * mm, "end": v(3.67, 39.22) * mm});
            skLineSegment(sketch, "E28.29.1", {"start": v(1.93, 36.8) * mm, "end": v(2.43, 36.77) * mm});
            skLineSegment(sketch, "E28.29.2", {"start": v(2, 36.8) * mm, "end": v(1.5, 36.82) * mm});
            skLineSegment(sketch, "E28.29.3", {"start": v(1.5, 36.82) * mm, "end": v(0.52, 39.4) * mm});
            skArc(sketch, "E28.29.4", {"start": v(0.15, 39.65) * mm, "mid": v(0.37, 39.58) * mm, "end": v(0.52, 39.4) * mm});
            skLineSegment(sketch, "E28.29.5", {"start": v(0.15, 39.7) * mm, "end": v(0.15, 39.65) * mm});
            skLineSegment(sketch, "E28.29.6", {"start": v(2.15, 39.6) * mm, "end": v(0.15, 39.7) * mm});
            skLineSegment(sketch, "E28.29.7", {"start": v(2.07, 39.6) * mm, "end": v(4.07, 39.5) * mm});
            skLineSegment(sketch, "E28.29.8", {"start": v(4.07, 39.5) * mm, "end": v(4.07, 39.44) * mm});
            skArc(sketch, "E28.29.9", {"start": v(4.07, 39.44) * mm, "mid": v(3.83, 39.4) * mm, "end": v(3.67, 39.22) * mm});
            skLineSegment(sketch, "E28.30.0", {"start": v(-1.5, 36.82) * mm, "end": v(-0.52, 39.4) * mm});
            skLineSegment(sketch, "E28.30.1", {"start": v(-2, 36.8) * mm, "end": v(-1.5, 36.82) * mm});
            skLineSegment(sketch, "E28.30.2", {"start": v(-1.93, 36.8) * mm, "end": v(-2.43, 36.77) * mm});
            skLineSegment(sketch, "E28.30.3", {"start": v(-2.43, 36.77) * mm, "end": v(-3.67, 39.22) * mm});
            skArc(sketch, "E28.30.4", {"start": v(-4.07, 39.44) * mm, "mid": v(-3.83, 39.4) * mm, "end": v(-3.67, 39.22) * mm});
            skLineSegment(sketch, "E28.30.5", {"start": v(-4.07, 39.5) * mm, "end": v(-4.07, 39.44) * mm});
            skLineSegment(sketch, "E28.30.6", {"start": v(-2.07, 39.6) * mm, "end": v(-4.07, 39.5) * mm});
            skLineSegment(sketch, "E28.30.7", {"start": v(-2.15, 39.6) * mm, "end": v(-0.15, 39.7) * mm});
            skLineSegment(sketch, "E28.30.8", {"start": v(-0.15, 39.7) * mm, "end": v(-0.15, 39.65) * mm});
            skArc(sketch, "E28.30.9", {"start": v(-0.15, 39.65) * mm, "mid": v(-0.37, 39.58) * mm, "end": v(-0.52, 39.4) * mm});
            skLineSegment(sketch, "E28.31.0", {"start": v(-5.4, 36.45) * mm, "end": v(-4.7, 39.11) * mm});
            skLineSegment(sketch, "E28.31.1", {"start": v(-5.9, 36.38) * mm, "end": v(-5.4, 36.45) * mm});
            skLineSegment(sketch, "E28.31.2", {"start": v(-5.83, 36.39) * mm, "end": v(-6.32, 36.3) * mm});
            skLineSegment(sketch, "E28.31.3", {"start": v(-6.32, 36.3) * mm, "end": v(-7.82, 38.61) * mm});
            skArc(sketch, "E28.31.4", {"start": v(-8.24, 38.79) * mm, "mid": v(-8, 38.76) * mm, "end": v(-7.82, 38.61) * mm});
            skLineSegment(sketch, "E28.31.5", {"start": v(-8.24, 38.83) * mm, "end": v(-8.24, 38.79) * mm});
            skLineSegment(sketch, "E28.31.6", {"start": v(-6.27, 39.15) * mm, "end": v(-8.24, 38.83) * mm});
            skLineSegment(sketch, "E28.31.7", {"start": v(-6.34, 39.14) * mm, "end": v(-4.37, 39.46) * mm});
            skLineSegment(sketch, "E28.31.8", {"start": v(-4.37, 39.46) * mm, "end": v(-4.36, 39.4) * mm});
            skArc(sketch, "E28.31.9", {"start": v(-4.36, 39.4) * mm, "mid": v(-4.58, 39.31) * mm, "end": v(-4.7, 39.11) * mm});
            skLineSegment(sketch, "E28.32.0", {"start": v(-9.25, 35.67) * mm, "end": v(-8.84, 38.4) * mm});
            skLineSegment(sketch, "E28.32.1", {"start": v(-9.73, 35.54) * mm, "end": v(-9.25, 35.67) * mm});
            skLineSegment(sketch, "E28.32.2", {"start": v(-9.66, 35.56) * mm, "end": v(-10.14, 35.43) * mm});
            skLineSegment(sketch, "E28.32.3", {"start": v(-10.14, 35.43) * mm, "end": v(-11.88, 37.56) * mm});
            skArc(sketch, "E28.32.4", {"start": v(-12.31, 37.69) * mm, "mid": v(-12.08, 37.7) * mm, "end": v(-11.88, 37.56) * mm});
            skLineSegment(sketch, "E28.32.5", {"start": v(-12.33, 37.74) * mm, "end": v(-12.31, 37.69) * mm});
            skLineSegment(sketch, "E28.32.6", {"start": v(-10.4, 38.26) * mm, "end": v(-12.33, 37.74) * mm});
            skLineSegment(sketch, "E28.32.7", {"start": v(-10.47, 38.24) * mm, "end": v(-8.54, 38.77) * mm});
            skLineSegment(sketch, "E28.32.8", {"start": v(-8.54, 38.77) * mm, "end": v(-8.53, 38.72) * mm});
            skArc(sketch, "E28.32.9", {"start": v(-8.53, 38.72) * mm, "mid": v(-8.73, 38.6) * mm, "end": v(-8.84, 38.4) * mm});
            skLineSegment(sketch, "E28.33.0", {"start": v(-12.99, 34.49) * mm, "end": v(-12.87, 37.24) * mm});
            skLineSegment(sketch, "E28.33.1", {"start": v(-13.45, 34.3) * mm, "end": v(-12.99, 34.49) * mm});
            skLineSegment(sketch, "E28.33.2", {"start": v(-13.39, 34.33) * mm, "end": v(-13.85, 34.15) * mm});
            skLineSegment(sketch, "E28.33.3", {"start": v(-13.85, 34.15) * mm, "end": v(-15.8, 36.09) * mm});
            skArc(sketch, "E28.33.4", {"start": v(-16.25, 36.17) * mm, "mid": v(-16.01, 36.2) * mm, "end": v(-15.8, 36.09) * mm});
            skLineSegment(sketch, "E28.33.5", {"start": v(-16.27, 36.21) * mm, "end": v(-16.25, 36.17) * mm});
            skLineSegment(sketch, "E28.33.6", {"start": v(-14.4, 36.94) * mm, "end": v(-16.27, 36.21) * mm});
            skLineSegment(sketch, "E28.33.7", {"start": v(-14.47, 36.91) * mm, "end": v(-12.61, 37.64) * mm});
            skLineSegment(sketch, "E28.33.8", {"start": v(-12.61, 37.64) * mm, "end": v(-12.6, 37.6) * mm});
            skArc(sketch, "E28.33.9", {"start": v(-12.6, 37.6) * mm, "mid": v(-12.79, 37.46) * mm, "end": v(-12.87, 37.24) * mm});
            skLineSegment(sketch, "E28.34.0", {"start": v(-16.58, 32.91) * mm, "end": v(-16.75, 35.66) * mm});
            skLineSegment(sketch, "E28.34.1", {"start": v(-17.02, 32.68) * mm, "end": v(-16.58, 32.91) * mm});
            skLineSegment(sketch, "E28.34.2", {"start": v(-16.96, 32.72) * mm, "end": v(-17.4, 32.48) * mm});
            skLineSegment(sketch, "E28.34.3", {"start": v(-17.4, 32.48) * mm, "end": v(-19.55, 34.2) * mm});
            skArc(sketch, "E28.34.4", {"start": v(-20, 34.24) * mm, "mid": v(-19.77, 34.29) * mm, "end": v(-19.55, 34.2) * mm});
            skLineSegment(sketch, "E28.34.5", {"start": v(-20.02, 34.28) * mm, "end": v(-20, 34.24) * mm});
            skLineSegment(sketch, "E28.34.6", {"start": v(-18.25, 35.2) * mm, "end": v(-20.02, 34.28) * mm});
            skLineSegment(sketch, "E28.34.7", {"start": v(-18.32, 35.17) * mm, "end": v(-16.54, 36.09) * mm});
            skLineSegment(sketch, "E28.34.8", {"start": v(-16.54, 36.09) * mm, "end": v(-16.52, 36.05) * mm});
            skArc(sketch, "E28.34.9", {"start": v(-16.52, 36.05) * mm, "mid": v(-16.7, 35.89) * mm, "end": v(-16.75, 35.66) * mm});
            skLineSegment(sketch, "E28.35.0", {"start": v(-19.98, 30.96) * mm, "end": v(-20.45, 33.67) * mm});
            skLineSegment(sketch, "E28.35.1", {"start": v(-20.4, 30.69) * mm, "end": v(-19.98, 30.96) * mm});
            skLineSegment(sketch, "E28.35.2", {"start": v(-20.34, 30.73) * mm, "end": v(-20.76, 30.45) * mm});
            skLineSegment(sketch, "E28.35.3", {"start": v(-20.76, 30.45) * mm, "end": v(-23.07, 31.93) * mm});
            skArc(sketch, "E28.35.4", {"start": v(-23.53, 31.92) * mm, "mid": v(-23.3, 32) * mm, "end": v(-23.07, 31.93) * mm});
            skLineSegment(sketch, "E28.35.5", {"start": v(-23.55, 31.96) * mm, "end": v(-23.53, 31.92) * mm});
            skLineSegment(sketch, "E28.35.6", {"start": v(-21.89, 33.06) * mm, "end": v(-23.55, 31.96) * mm});
            skLineSegment(sketch, "E28.35.7", {"start": v(-21.95, 33.02) * mm, "end": v(-20.28, 34.13) * mm});
            skLineSegment(sketch, "E28.35.8", {"start": v(-20.28, 34.13) * mm, "end": v(-20.26, 34.09) * mm});
            skArc(sketch, "E28.35.9", {"start": v(-20.26, 34.09) * mm, "mid": v(-20.42, 33.9) * mm, "end": v(-20.45, 33.67) * mm});
            skLineSegment(sketch, "E28.36.0", {"start": v(-23.16, 28.67) * mm, "end": v(-23.9, 31.3) * mm});
            skLineSegment(sketch, "E28.36.1", {"start": v(-23.55, 28.35) * mm, "end": v(-23.16, 28.67) * mm});
            skLineSegment(sketch, "E28.36.2", {"start": v(-23.5, 28.4) * mm, "end": v(-23.88, 28.07) * mm});
            skLineSegment(sketch, "E28.36.3", {"start": v(-23.88, 28.07) * mm, "end": v(-26.34, 29.3) * mm});
            skArc(sketch, "E28.36.4", {"start": v(-26.79, 29.23) * mm, "mid": v(-26.57, 29.34) * mm, "end": v(-26.34, 29.3) * mm});
            skLineSegment(sketch, "E28.36.5", {"start": v(-26.82, 29.27) * mm, "end": v(-26.79, 29.23) * mm});
            skLineSegment(sketch, "E28.36.6", {"start": v(-25.28, 30.55) * mm, "end": v(-26.82, 29.27) * mm});
            skLineSegment(sketch, "E28.36.7", {"start": v(-25.34, 30.5) * mm, "end": v(-23.8, 31.78) * mm});
            skLineSegment(sketch, "E28.36.8", {"start": v(-23.8, 31.78) * mm, "end": v(-23.76, 31.74) * mm});
            skArc(sketch, "E28.36.9", {"start": v(-23.76, 31.74) * mm, "mid": v(-23.9, 31.55) * mm, "end": v(-23.9, 31.3) * mm});
            skLineSegment(sketch, "E28.37.0", {"start": v(-26.08, 26.04) * mm, "end": v(-27.1, 28.6) * mm});
            skLineSegment(sketch, "E28.37.1", {"start": v(-26.43, 25.68) * mm, "end": v(-26.08, 26.04) * mm});
            skLineSegment(sketch, "E28.37.2", {"start": v(-26.38, 25.73) * mm, "end": v(-26.73, 25.37) * mm});
            skLineSegment(sketch, "E28.37.3", {"start": v(-26.73, 25.37) * mm, "end": v(-29.3, 26.33) * mm});
            skArc(sketch, "E28.37.4", {"start": v(-29.74, 26.22) * mm, "mid": v(-29.54, 26.34) * mm, "end": v(-29.3, 26.33) * mm});
            skLineSegment(sketch, "E28.37.5", {"start": v(-29.78, 26.26) * mm, "end": v(-29.74, 26.22) * mm});
            skLineSegment(sketch, "E28.37.6", {"start": v(-28.38, 27.69) * mm, "end": v(-29.78, 26.26) * mm});
            skLineSegment(sketch, "E28.37.7", {"start": v(-28.43, 27.63) * mm, "end": v(-27.04, 29.07) * mm});
            skLineSegment(sketch, "E28.37.8", {"start": v(-27.04, 29.07) * mm, "end": v(-27, 29.03) * mm});
            skArc(sketch, "E28.37.9", {"start": v(-27, 29.03) * mm, "mid": v(-27.12, 28.83) * mm, "end": v(-27.1, 28.6) * mm});
            skLineSegment(sketch, "E28.38.0", {"start": v(-28.7, 23.12) * mm, "end": v(-29.99, 25.55) * mm});
            skLineSegment(sketch, "E28.38.1", {"start": v(-29, 22.73) * mm, "end": v(-28.7, 23.12) * mm});
            skLineSegment(sketch, "E28.38.2", {"start": v(-28.96, 22.78) * mm, "end": v(-29.27, 22.4) * mm});
            skLineSegment(sketch, "E28.38.3", {"start": v(-29.27, 22.4) * mm, "end": v(-31.94, 23.07) * mm});
            skArc(sketch, "E28.38.4", {"start": v(-32.36, 22.91) * mm, "mid": v(-32.17, 23.06) * mm, "end": v(-31.94, 23.07) * mm});
            skLineSegment(sketch, "E28.38.5", {"start": v(-32.4, 22.94) * mm, "end": v(-32.36, 22.91) * mm});
            skLineSegment(sketch, "E28.38.6", {"start": v(-31.16, 24.51) * mm, "end": v(-32.4, 22.94) * mm});
            skLineSegment(sketch, "E28.38.7", {"start": v(-31.21, 24.46) * mm, "end": v(-29.98, 26.03) * mm});
            skLineSegment(sketch, "E28.38.8", {"start": v(-29.98, 26.03) * mm, "end": v(-29.94, 26) * mm});
            skArc(sketch, "E28.38.9", {"start": v(-29.94, 26) * mm, "mid": v(-30.03, 25.78) * mm, "end": v(-29.99, 25.55) * mm});
            skLineSegment(sketch, "E28.39.0", {"start": v(-31, 19.94) * mm, "end": v(-32.53, 22.22) * mm});
            skLineSegment(sketch, "E28.39.1", {"start": v(-31.26, 19.52) * mm, "end": v(-31, 19.94) * mm});
            skLineSegment(sketch, "E28.39.2", {"start": v(-31.22, 19.58) * mm, "end": v(-31.49, 19.15) * mm});
            skLineSegment(sketch, "E28.39.3", {"start": v(-31.49, 19.15) * mm, "end": v(-34.2, 19.54) * mm});
            skArc(sketch, "E28.39.4", {"start": v(-34.61, 19.34) * mm, "mid": v(-34.44, 19.5) * mm, "end": v(-34.2, 19.54) * mm});
            skLineSegment(sketch, "E28.39.5", {"start": v(-34.66, 19.37) * mm, "end": v(-34.61, 19.34) * mm});
            skLineSegment(sketch, "E28.39.6", {"start": v(-33.6, 21.06) * mm, "end": v(-34.66, 19.37) * mm});
            skLineSegment(sketch, "E28.39.7", {"start": v(-33.63, 21) * mm, "end": v(-32.57, 22.7) * mm});
            skLineSegment(sketch, "E28.39.8", {"start": v(-32.57, 22.7) * mm, "end": v(-32.53, 22.67) * mm});
            skArc(sketch, "E28.39.9", {"start": v(-32.53, 22.67) * mm, "mid": v(-32.6, 22.44) * mm, "end": v(-32.53, 22.22) * mm});
            skLineSegment(sketch, "E28.40.0", {"start": v(-32.94, 16.53) * mm, "end": v(-34.71, 18.63) * mm});
            skLineSegment(sketch, "E28.40.1", {"start": v(-33.16, 16.08) * mm, "end": v(-32.94, 16.53) * mm});
            skLineSegment(sketch, "E28.40.2", {"start": v(-33.12, 16.15) * mm, "end": v(-33.34, 15.7) * mm});
            skLineSegment(sketch, "E28.40.3", {"start": v(-33.34, 15.7) * mm, "end": v(-36.09, 15.8) * mm});
            skArc(sketch, "E28.40.4", {"start": v(-36.47, 15.55) * mm, "mid": v(-36.32, 15.73) * mm, "end": v(-36.09, 15.8) * mm});
            skLineSegment(sketch, "E28.40.5", {"start": v(-36.52, 15.58) * mm, "end": v(-36.47, 15.55) * mm});
            skLineSegment(sketch, "E28.40.6", {"start": v(-35.64, 17.37) * mm, "end": v(-36.52, 15.58) * mm});
            skLineSegment(sketch, "E28.40.7", {"start": v(-35.67, 17.3) * mm, "end": v(-34.8, 19.1) * mm});
            skLineSegment(sketch, "E28.40.8", {"start": v(-34.8, 19.1) * mm, "end": v(-34.76, 19.08) * mm});
            skArc(sketch, "E28.40.9", {"start": v(-34.76, 19.08) * mm, "mid": v(-34.8, 18.85) * mm, "end": v(-34.71, 18.63) * mm});
            skLineSegment(sketch, "E28.41.0", {"start": v(-34.5, 12.94) * mm, "end": v(-36.5, 14.84) * mm});
            skLineSegment(sketch, "E28.41.1", {"start": v(-34.68, 12.47) * mm, "end": v(-34.5, 12.94) * mm});
            skLineSegment(sketch, "E28.41.2", {"start": v(-34.65, 12.53) * mm, "end": v(-34.82, 12.06) * mm});
            skLineSegment(sketch, "E28.41.3", {"start": v(-34.82, 12.06) * mm, "end": v(-37.56, 11.87) * mm});
            skArc(sketch, "E28.41.4", {"start": v(-37.92, 11.59) * mm, "mid": v(-37.79, 11.78) * mm, "end": v(-37.56, 11.87) * mm});
            skLineSegment(sketch, "E28.41.5", {"start": v(-37.97, 11.6) * mm, "end": v(-37.92, 11.59) * mm});
            skLineSegment(sketch, "E28.41.6", {"start": v(-37.29, 13.49) * mm, "end": v(-37.97, 11.6) * mm});
            skLineSegment(sketch, "E28.41.7", {"start": v(-37.31, 13.42) * mm, "end": v(-36.63, 15.3) * mm});
            skLineSegment(sketch, "E28.41.8", {"start": v(-36.63, 15.3) * mm, "end": v(-36.59, 15.28) * mm});
            skArc(sketch, "E28.41.9", {"start": v(-36.59, 15.28) * mm, "mid": v(-36.6, 15.04) * mm, "end": v(-36.5, 14.84) * mm});
            skLineSegment(sketch, "E28.42.0", {"start": v(-35.69, 9.2) * mm, "end": v(-37.86, 10.87) * mm});
            skLineSegment(sketch, "E28.42.1", {"start": v(-35.8, 8.71) * mm, "end": v(-35.69, 9.2) * mm});
            skLineSegment(sketch, "E28.42.2", {"start": v(-35.79, 8.78) * mm, "end": v(-35.9, 8.3) * mm});
            skLineSegment(sketch, "E28.42.3", {"start": v(-35.9, 8.3) * mm, "end": v(-38.61, 7.81) * mm});
            skArc(sketch, "E28.42.4", {"start": v(-38.94, 7.5) * mm, "mid": v(-38.82, 7.7) * mm, "end": v(-38.61, 7.81) * mm});
            skLineSegment(sketch, "E28.42.5", {"start": v(-38.98, 7.5) * mm, "end": v(-38.94, 7.5) * mm});
            skLineSegment(sketch, "E28.42.6", {"start": v(-38.5, 9.45) * mm, "end": v(-38.98, 7.5) * mm});
            skLineSegment(sketch, "E28.42.7", {"start": v(-38.53, 9.37) * mm, "end": v(-38.05, 11.32) * mm});
            skLineSegment(sketch, "E28.42.8", {"start": v(-38.05, 11.32) * mm, "end": v(-38, 11.3) * mm});
            skArc(sketch, "E28.42.9", {"start": v(-38, 11.3) * mm, "mid": v(-38, 11.07) * mm, "end": v(-37.86, 10.87) * mm});
            skLineSegment(sketch, "E28.43.0", {"start": v(-36.46, 5.35) * mm, "end": v(-38.8, 6.79) * mm});
            skLineSegment(sketch, "E28.43.1", {"start": v(-36.53, 4.86) * mm, "end": v(-36.46, 5.35) * mm});
            skLineSegment(sketch, "E28.43.2", {"start": v(-36.52, 4.93) * mm, "end": v(-36.59, 4.43) * mm});
            skLineSegment(sketch, "E28.43.3", {"start": v(-36.59, 4.43) * mm, "end": v(-39.22, 3.66) * mm});
            skArc(sketch, "E28.43.4", {"start": v(-39.51, 3.31) * mm, "mid": v(-39.42, 3.53) * mm, "end": v(-39.22, 3.66) * mm});
            skLineSegment(sketch, "E28.43.5", {"start": v(-39.56, 3.32) * mm, "end": v(-39.51, 3.31) * mm});
            skLineSegment(sketch, "E28.43.6", {"start": v(-39.3, 5.3) * mm, "end": v(-39.56, 3.32) * mm});
            skLineSegment(sketch, "E28.43.7", {"start": v(-39.3, 5.23) * mm, "end": v(-39.04, 7.2) * mm});
            skLineSegment(sketch, "E28.43.8", {"start": v(-39.04, 7.2) * mm, "end": v(-39, 7.2) * mm});
            skArc(sketch, "E28.43.9", {"start": v(-39, 7.2) * mm, "mid": v(-38.96, 6.97) * mm, "end": v(-38.8, 6.79) * mm});
            skLineSegment(sketch, "E28.44.0", {"start": v(-36.82, 1.45) * mm, "end": v(-39.3, 2.62) * mm});
            skLineSegment(sketch, "E28.44.1", {"start": v(-36.84, 0.95) * mm, "end": v(-36.82, 1.45) * mm});
            skLineSegment(sketch, "E28.44.2", {"start": v(-36.84, 1.02) * mm, "end": v(-36.85, 0.52) * mm});
            skLineSegment(sketch, "E28.44.3", {"start": v(-36.85, 0.52) * mm, "end": v(-39.4, -0.53) * mm});
            skArc(sketch, "E28.44.4", {"start": v(-39.64, -0.9) * mm, "mid": v(-39.57, -0.68) * mm, "end": v(-39.4, -0.53) * mm});
            skLineSegment(sketch, "E28.44.5", {"start": v(-39.7, -0.9) * mm, "end": v(-39.64, -0.9) * mm});
            skLineSegment(sketch, "E28.44.6", {"start": v(-39.63, 1.1) * mm, "end": v(-39.7, -0.9) * mm});
            skLineSegment(sketch, "E28.44.7", {"start": v(-39.64, 1.02) * mm, "end": v(-39.59, 3.02) * mm});
            skLineSegment(sketch, "E28.44.8", {"start": v(-39.59, 3.02) * mm, "end": v(-39.54, 3.02) * mm});
            skArc(sketch, "E28.44.9", {"start": v(-39.54, 3.02) * mm, "mid": v(-39.48, 2.78) * mm, "end": v(-39.3, 2.62) * mm});
            skLineSegment(sketch, "E28.45.0", {"start": v(-36.77, -2.48) * mm, "end": v(-39.36, -1.57) * mm});
            skLineSegment(sketch, "E28.45.1", {"start": v(-36.73, -2.98) * mm, "end": v(-36.77, -2.48) * mm});
            skLineSegment(sketch, "E28.45.2", {"start": v(-36.74, -2.9) * mm, "end": v(-36.7, -3.4) * mm});
            skLineSegment(sketch, "E28.45.3", {"start": v(-36.7, -3.4) * mm, "end": v(-39.11, -4.71) * mm});
            skArc(sketch, "E28.45.4", {"start": v(-39.32, -5.12) * mm, "mid": v(-39.28, -4.88) * mm, "end": v(-39.11, -4.71) * mm});
            skLineSegment(sketch, "E28.45.5", {"start": v(-39.37, -5.12) * mm, "end": v(-39.32, -5.12) * mm});
            skLineSegment(sketch, "E28.45.6", {"start": v(-39.53, -3.13) * mm, "end": v(-39.37, -5.12) * mm});
            skLineSegment(sketch, "E28.45.7", {"start": v(-39.52, -3.2) * mm, "end": v(-39.68, -1.2) * mm});
            skLineSegment(sketch, "E28.45.8", {"start": v(-39.68, -1.2) * mm, "end": v(-39.63, -1.2) * mm});
            skArc(sketch, "E28.45.9", {"start": v(-39.63, -1.2) * mm, "mid": v(-39.55, -1.43) * mm, "end": v(-39.36, -1.57) * mm});
            skLineSegment(sketch, "E28.46.0", {"start": v(-36.3, -6.37) * mm, "end": v(-38.97, -5.74) * mm});
            skLineSegment(sketch, "E28.46.1", {"start": v(-36.2, -6.86) * mm, "end": v(-36.3, -6.37) * mm});
            skLineSegment(sketch, "E28.46.2", {"start": v(-36.22, -6.8) * mm, "end": v(-36.13, -7.28) * mm});
            skLineSegment(sketch, "E28.46.3", {"start": v(-36.13, -7.28) * mm, "end": v(-38.39, -8.84) * mm});
            skArc(sketch, "E28.46.4", {"start": v(-38.55, -9.27) * mm, "mid": v(-38.54, -9.03) * mm, "end": v(-38.39, -8.84) * mm});
            skLineSegment(sketch, "E28.46.5", {"start": v(-38.6, -9.28) * mm, "end": v(-38.55, -9.27) * mm});
            skLineSegment(sketch, "E28.46.6", {"start": v(-38.97, -7.3) * mm, "end": v(-38.6, -9.28) * mm});
            skLineSegment(sketch, "E28.46.7", {"start": v(-38.96, -7.38) * mm, "end": v(-39.33, -5.42) * mm});
            skLineSegment(sketch, "E28.46.8", {"start": v(-39.33, -5.42) * mm, "end": v(-39.28, -5.4) * mm});
            skArc(sketch, "E28.46.9", {"start": v(-39.28, -5.4) * mm, "mid": v(-39.18, -5.62) * mm, "end": v(-38.97, -5.74) * mm});
            skLineSegment(sketch, "E28.47.0", {"start": v(-35.42, -10.2) * mm, "end": v(-38.14, -9.85) * mm});
            skLineSegment(sketch, "E28.47.1", {"start": v(-35.27, -10.67) * mm, "end": v(-35.42, -10.2) * mm});
            skLineSegment(sketch, "E28.47.2", {"start": v(-35.3, -10.6) * mm, "end": v(-35.15, -11.08) * mm});
            skLineSegment(sketch, "E28.47.3", {"start": v(-35.15, -11.08) * mm, "end": v(-37.23, -12.87) * mm});
            skArc(sketch, "E28.47.4", {"start": v(-37.35, -13.31) * mm, "mid": v(-37.36, -13.07) * mm, "end": v(-37.23, -12.87) * mm});
            skLineSegment(sketch, "E28.47.5", {"start": v(-37.4, -13.33) * mm, "end": v(-37.35, -13.31) * mm});
            skLineSegment(sketch, "E28.47.6", {"start": v(-37.97, -11.41) * mm, "end": v(-37.4, -13.33) * mm});
            skLineSegment(sketch, "E28.47.7", {"start": v(-37.95, -11.48) * mm, "end": v(-38.53, -9.57) * mm});
            skLineSegment(sketch, "E28.47.8", {"start": v(-38.53, -9.57) * mm, "end": v(-38.48, -9.55) * mm});
            skArc(sketch, "E28.47.9", {"start": v(-38.48, -9.55) * mm, "mid": v(-38.36, -9.76) * mm, "end": v(-38.14, -9.85) * mm});
            skLineSegment(sketch, "E28.48.0", {"start": v(-34.13, -13.9) * mm, "end": v(-36.88, -13.85) * mm});
            skLineSegment(sketch, "E28.48.1", {"start": v(-33.94, -14.36) * mm, "end": v(-34.13, -13.9) * mm});
            skLineSegment(sketch, "E28.48.2", {"start": v(-33.96, -14.3) * mm, "end": v(-33.77, -14.76) * mm});
            skLineSegment(sketch, "E28.48.3", {"start": v(-33.77, -14.76) * mm, "end": v(-35.65, -16.76) * mm});
            skArc(sketch, "E28.48.4", {"start": v(-35.72, -17.2) * mm, "mid": v(-35.76, -16.97) * mm, "end": v(-35.65, -16.76) * mm});
            skLineSegment(sketch, "E28.48.5", {"start": v(-35.77, -17.23) * mm, "end": v(-35.72, -17.2) * mm});
            skLineSegment(sketch, "E28.48.6", {"start": v(-36.54, -15.38) * mm, "end": v(-35.77, -17.23) * mm});
            skLineSegment(sketch, "E28.48.7", {"start": v(-36.52, -15.45) * mm, "end": v(-37.3, -13.6) * mm});
            skLineSegment(sketch, "E28.48.8", {"start": v(-37.3, -13.6) * mm, "end": v(-37.25, -13.6) * mm});
            skArc(sketch, "E28.48.9", {"start": v(-37.25, -13.6) * mm, "mid": v(-37.1, -13.78) * mm, "end": v(-36.88, -13.85) * mm});
            skLineSegment(sketch, "E28.49.0", {"start": v(-32.46, -17.45) * mm, "end": v(-35.2, -17.7) * mm});
            skLineSegment(sketch, "E28.49.1", {"start": v(-32.22, -17.89) * mm, "end": v(-32.46, -17.45) * mm});
            skLineSegment(sketch, "E28.49.2", {"start": v(-32.25, -17.82) * mm, "end": v(-32, -18.26) * mm});
            skLineSegment(sketch, "E28.49.3", {"start": v(-32, -18.26) * mm, "end": v(-33.67, -20.45) * mm});
            skArc(sketch, "E28.49.4", {"start": v(-33.7, -20.9) * mm, "mid": v(-33.75, -20.68) * mm, "end": v(-33.67, -20.45) * mm});
            skLineSegment(sketch, "E28.49.5", {"start": v(-33.74, -20.93) * mm, "end": v(-33.7, -20.9) * mm});
            skLineSegment(sketch, "E28.49.6", {"start": v(-34.7, -19.18) * mm, "end": v(-33.74, -20.93) * mm});
            skLineSegment(sketch, "E28.49.7", {"start": v(-34.67, -19.25) * mm, "end": v(-35.64, -17.5) * mm});
            skLineSegment(sketch, "E28.49.8", {"start": v(-35.64, -17.5) * mm, "end": v(-35.6, -17.47) * mm});
            skArc(sketch, "E28.49.9", {"start": v(-35.6, -17.47) * mm, "mid": v(-35.43, -17.64) * mm, "end": v(-35.2, -17.7) * mm});
            skLineSegment(sketch, "E28.50.0", {"start": v(-30.42, -20.8) * mm, "end": v(-33.12, -21.34) * mm});
            skLineSegment(sketch, "E28.50.1", {"start": v(-30.13, -21.2) * mm, "end": v(-30.42, -20.8) * mm});
            skLineSegment(sketch, "E28.50.2", {"start": v(-30.17, -21.15) * mm, "end": v(-29.89, -21.56) * mm});
            skLineSegment(sketch, "E28.50.3", {"start": v(-29.89, -21.56) * mm, "end": v(-31.3, -23.92) * mm});
            skArc(sketch, "E28.50.4", {"start": v(-31.28, -24.37) * mm, "mid": v(-31.36, -24.15) * mm, "end": v(-31.3, -23.92) * mm});
            skLineSegment(sketch, "E28.50.5", {"start": v(-31.32, -24.4) * mm, "end": v(-31.28, -24.37) * mm});
            skLineSegment(sketch, "E28.50.6", {"start": v(-32.47, -22.76) * mm, "end": v(-31.32, -24.4) * mm});
            skLineSegment(sketch, "E28.50.7", {"start": v(-32.42, -22.82) * mm, "end": v(-33.58, -21.19) * mm});
            skLineSegment(sketch, "E28.50.8", {"start": v(-33.58, -21.19) * mm, "end": v(-33.53, -21.16) * mm});
            skArc(sketch, "E28.50.9", {"start": v(-33.53, -21.16) * mm, "mid": v(-33.35, -21.31) * mm, "end": v(-33.12, -21.34) * mm});
            skLineSegment(sketch, "E28.51.0", {"start": v(-28.04, -23.92) * mm, "end": v(-30.66, -24.73) * mm});
            skLineSegment(sketch, "E28.51.1", {"start": v(-27.7, -24.3) * mm, "end": v(-28.04, -23.92) * mm});
            skLineSegment(sketch, "E28.51.2", {"start": v(-27.76, -24.24) * mm, "end": v(-27.43, -24.62) * mm});
            skLineSegment(sketch, "E28.51.3", {"start": v(-27.43, -24.62) * mm, "end": v(-28.59, -27.1) * mm});
            skArc(sketch, "E28.51.4", {"start": v(-28.51, -27.55) * mm, "mid": v(-28.62, -27.34) * mm, "end": v(-28.59, -27.1) * mm});
            skLineSegment(sketch, "E28.51.5", {"start": v(-28.55, -27.59) * mm, "end": v(-28.51, -27.55) * mm});
            skLineSegment(sketch, "E28.51.6", {"start": v(-29.86, -26.08) * mm, "end": v(-28.55, -27.59) * mm});
            skLineSegment(sketch, "E28.51.7", {"start": v(-29.81, -26.14) * mm, "end": v(-31.13, -24.63) * mm});
            skLineSegment(sketch, "E28.51.8", {"start": v(-31.13, -24.63) * mm, "end": v(-31.1, -24.6) * mm});
            skArc(sketch, "E28.51.9", {"start": v(-31.1, -24.6) * mm, "mid": v(-30.9, -24.74) * mm, "end": v(-30.66, -24.73) * mm});
            skLineSegment(sketch, "E28.52.0", {"start": v(-25.34, -26.76) * mm, "end": v(-27.86, -27.85) * mm});
            skLineSegment(sketch, "E28.52.1", {"start": v(-24.97, -27.1) * mm, "end": v(-25.34, -26.76) * mm});
            skLineSegment(sketch, "E28.52.2", {"start": v(-25.02, -27.05) * mm, "end": v(-24.65, -27.4) * mm});
            skLineSegment(sketch, "E28.52.3", {"start": v(-24.65, -27.4) * mm, "end": v(-25.54, -30) * mm});
            skArc(sketch, "E28.52.4", {"start": v(-25.42, -30.43) * mm, "mid": v(-25.55, -30.23) * mm, "end": v(-25.54, -30) * mm});
            skLineSegment(sketch, "E28.52.5", {"start": v(-25.45, -30.47) * mm, "end": v(-25.42, -30.43) * mm});
            skLineSegment(sketch, "E28.52.6", {"start": v(-26.92, -29.1) * mm, "end": v(-25.45, -30.47) * mm});
            skLineSegment(sketch, "E28.52.7", {"start": v(-26.87, -29.16) * mm, "end": v(-28.34, -27.8) * mm});
            skLineSegment(sketch, "E28.52.8", {"start": v(-28.34, -27.8) * mm, "end": v(-28.3, -27.77) * mm});
            skArc(sketch, "E28.52.9", {"start": v(-28.3, -27.77) * mm, "mid": v(-28.1, -27.88) * mm, "end": v(-27.86, -27.85) * mm});
            skLineSegment(sketch, "E28.53.0", {"start": v(-22.35, -29.3) * mm, "end": v(-24.74, -30.66) * mm});
            skLineSegment(sketch, "E28.53.1", {"start": v(-21.95, -29.6) * mm, "end": v(-22.35, -29.3) * mm});
            skLineSegment(sketch, "E28.53.2", {"start": v(-22, -29.56) * mm, "end": v(-21.6, -29.86) * mm});
            skLineSegment(sketch, "E28.53.3", {"start": v(-21.6, -29.86) * mm, "end": v(-22.2, -32.54) * mm});
            skArc(sketch, "E28.53.4", {"start": v(-22.04, -32.96) * mm, "mid": v(-22.2, -32.77) * mm, "end": v(-22.2, -32.54) * mm});
            skLineSegment(sketch, "E28.53.5", {"start": v(-22.07, -33) * mm, "end": v(-22.04, -32.96) * mm});
            skLineSegment(sketch, "E28.53.6", {"start": v(-23.68, -31.8) * mm, "end": v(-22.07, -33) * mm});
            skLineSegment(sketch, "E28.53.7", {"start": v(-23.62, -31.85) * mm, "end": v(-25.22, -30.66) * mm});
            skLineSegment(sketch, "E28.53.8", {"start": v(-25.22, -30.66) * mm, "end": v(-25.2, -30.62) * mm});
            skArc(sketch, "E28.53.9", {"start": v(-25.2, -30.62) * mm, "mid": v(-24.97, -30.7) * mm, "end": v(-24.74, -30.66) * mm});
            skLineSegment(sketch, "E28.54.0", {"start": v(-19.1, -31.51) * mm, "end": v(-21.34, -33.11) * mm});
            skLineSegment(sketch, "E28.54.1", {"start": v(-18.68, -31.77) * mm, "end": v(-19.1, -31.51) * mm});
            skLineSegment(sketch, "E28.54.2", {"start": v(-18.74, -31.73) * mm, "end": v(-18.3, -31.98) * mm});
            skLineSegment(sketch, "E28.54.3", {"start": v(-18.3, -31.98) * mm, "end": v(-18.63, -34.71) * mm});
            skArc(sketch, "E28.54.4", {"start": v(-18.41, -35.11) * mm, "mid": v(-18.58, -34.95) * mm, "end": v(-18.63, -34.71) * mm});
            skLineSegment(sketch, "E28.54.5", {"start": v(-18.44, -35.16) * mm, "end": v(-18.41, -35.11) * mm});
            skLineSegment(sketch, "E28.54.6", {"start": v(-20.16, -34.14) * mm, "end": v(-18.44, -35.16) * mm});
            skLineSegment(sketch, "E28.54.7", {"start": v(-20.1, -34.18) * mm, "end": v(-21.82, -33.17) * mm});
            skLineSegment(sketch, "E28.54.8", {"start": v(-21.82, -33.17) * mm, "end": v(-21.8, -33.12) * mm});
            skArc(sketch, "E28.54.9", {"start": v(-21.8, -33.12) * mm, "mid": v(-21.57, -33.19) * mm, "end": v(-21.34, -33.11) * mm});
            skLineSegment(sketch, "E28.55.0", {"start": v(-15.65, -33.36) * mm, "end": v(-17.7, -35.2) * mm});
            skLineSegment(sketch, "E28.55.1", {"start": v(-15.2, -33.57) * mm, "end": v(-15.65, -33.36) * mm});
            skLineSegment(sketch, "E28.55.2", {"start": v(-15.26, -33.54) * mm, "end": v(-14.8, -33.75) * mm});
            skLineSegment(sketch, "E28.55.3", {"start": v(-14.8, -33.75) * mm, "end": v(-14.83, -36.5) * mm});
            skArc(sketch, "E28.55.4", {"start": v(-14.58, -36.87) * mm, "mid": v(-14.76, -36.72) * mm, "end": v(-14.83, -36.5) * mm});
            skLineSegment(sketch, "E28.55.5", {"start": v(-14.6, -36.92) * mm, "end": v(-14.58, -36.87) * mm});
            skLineSegment(sketch, "E28.55.6", {"start": v(-16.42, -36.1) * mm, "end": v(-14.6, -36.92) * mm});
            skLineSegment(sketch, "E28.55.7", {"start": v(-16.35, -36.12) * mm, "end": v(-18.17, -35.3) * mm});
            skLineSegment(sketch, "E28.55.8", {"start": v(-18.17, -35.3) * mm, "end": v(-18.15, -35.25) * mm});
            skArc(sketch, "E28.55.9", {"start": v(-18.15, -35.25) * mm, "mid": v(-17.92, -35.3) * mm, "end": v(-17.7, -35.2) * mm});
            skLineSegment(sketch, "E28.56.0", {"start": v(-12.02, -34.84) * mm, "end": v(-13.86, -36.88) * mm});
            skLineSegment(sketch, "E28.56.1", {"start": v(-11.54, -35) * mm, "end": v(-12.02, -34.84) * mm});
            skLineSegment(sketch, "E28.56.2", {"start": v(-11.6, -34.97) * mm, "end": v(-11.13, -35.13) * mm});
            skLineSegment(sketch, "E28.56.3", {"start": v(-11.13, -35.13) * mm, "end": v(-10.87, -37.87) * mm});
            skArc(sketch, "E28.56.4", {"start": v(-10.57, -38.21) * mm, "mid": v(-10.77, -38.09) * mm, "end": v(-10.87, -37.87) * mm});
            skLineSegment(sketch, "E28.56.5", {"start": v(-10.6, -38.26) * mm, "end": v(-10.57, -38.21) * mm});
            skLineSegment(sketch, "E28.56.6", {"start": v(-12.49, -37.63) * mm, "end": v(-10.6, -38.26) * mm});
            skLineSegment(sketch, "E28.56.7", {"start": v(-12.42, -37.66) * mm, "end": v(-14.32, -37.03) * mm});
            skLineSegment(sketch, "E28.56.8", {"start": v(-14.32, -37.03) * mm, "end": v(-14.3, -36.98) * mm});
            skArc(sketch, "E28.56.9", {"start": v(-14.3, -36.98) * mm, "mid": v(-14.06, -37) * mm, "end": v(-13.86, -36.88) * mm});
            skLineSegment(sketch, "E28.57.0", {"start": v(-8.24, -35.92) * mm, "end": v(-9.86, -38.14) * mm});
            skLineSegment(sketch, "E28.57.1", {"start": v(-7.76, -36.02) * mm, "end": v(-8.24, -35.92) * mm});
            skLineSegment(sketch, "E28.57.2", {"start": v(-7.82, -36) * mm, "end": v(-7.34, -36.12) * mm});
            skLineSegment(sketch, "E28.57.3", {"start": v(-7.34, -36.12) * mm, "end": v(-6.78, -38.8) * mm});
            skArc(sketch, "E28.57.4", {"start": v(-6.45, -39.12) * mm, "mid": v(-6.67, -39.02) * mm, "end": v(-6.78, -38.8) * mm});
            skLineSegment(sketch, "E28.57.5", {"start": v(-6.46, -39.17) * mm, "end": v(-6.45, -39.12) * mm});
            skLineSegment(sketch, "E28.57.6", {"start": v(-8.42, -38.75) * mm, "end": v(-6.46, -39.17) * mm});
            skLineSegment(sketch, "E28.57.7", {"start": v(-8.34, -38.76) * mm, "end": v(-10.3, -38.34) * mm});
            skLineSegment(sketch, "E28.57.8", {"start": v(-10.3, -38.34) * mm, "end": v(-10.29, -38.3) * mm});
            skArc(sketch, "E28.57.9", {"start": v(-10.29, -38.3) * mm, "mid": v(-10.05, -38.28) * mm, "end": v(-9.86, -38.14) * mm});
            skLineSegment(sketch, "E28.58.0", {"start": v(-4.38, -36.6) * mm, "end": v(-5.75, -38.97) * mm});
            skLineSegment(sketch, "E28.58.1", {"start": v(-3.88, -36.64) * mm, "end": v(-4.38, -36.6) * mm});
            skLineSegment(sketch, "E28.58.2", {"start": v(-3.95, -36.64) * mm, "end": v(-3.45, -36.7) * mm});
            skLineSegment(sketch, "E28.58.3", {"start": v(-3.45, -36.7) * mm, "end": v(-2.62, -39.3) * mm});
            skArc(sketch, "E28.58.4", {"start": v(-2.26, -39.59) * mm, "mid": v(-2.48, -39.5) * mm, "end": v(-2.62, -39.3) * mm});
            skLineSegment(sketch, "E28.58.5", {"start": v(-2.26, -39.64) * mm, "end": v(-2.26, -39.59) * mm});
            skLineSegment(sketch, "E28.58.6", {"start": v(-4.25, -39.42) * mm, "end": v(-2.26, -39.64) * mm});
            skLineSegment(sketch, "E28.58.7", {"start": v(-4.18, -39.43) * mm, "end": v(-6.17, -39.22) * mm});
            skLineSegment(sketch, "E28.58.8", {"start": v(-6.17, -39.22) * mm, "end": v(-6.16, -39.17) * mm});
            skArc(sketch, "E28.58.9", {"start": v(-6.16, -39.17) * mm, "mid": v(-5.93, -39.13) * mm, "end": v(-5.75, -38.97) * mm});
            skPoint(sketch, "E28.center", {"position": v(0, 0) * mm});
            skSolve(sketch);
        }
        {
            var Q0;
            Q0=makeQuery(id+"F2.imprint","IMPRINT",FACE,{"disambiguationData":[TD([[makeQuery(id+"F2.imprint","IMPRINT",EDGE,{"derivedFrom":sQuery(id+"F2.wireOp",EDGE,"E28.56.0")}),1.0]])]});
            var Q1;
            Q1=makeQuery(id+"F2.imprint","IMPRINT",FACE,{"disambiguationData":[TD([[makeQuery(id+"F2.imprint","IMPRINT",EDGE,{"derivedFrom":sQuery(id+"F2.wireOp",EDGE,"E28.55.0")}),1.0]])]});
            var Q2;
            Q2=makeQuery(id+"F2.imprint","IMPRINT",FACE,{"disambiguationData":[TD([[makeQuery(id+"F2.imprint","IMPRINT",EDGE,{"derivedFrom":sQuery(id+"F2.wireOp",EDGE,"E28.54.0")}),1.0]])]});
            var Q3;
            Q3=makeQuery(id+"F2.imprint","IMPRINT",FACE,{"disambiguationData":[TD([[makeQuery(id+"F2.imprint","IMPRINT",EDGE,{"derivedFrom":sQuery(id+"F2.wireOp",EDGE,"E28.53.0")}),1.0]])]});
            var Q4;
            Q4=makeQuery(id+"F2.imprint","IMPRINT",FACE,{"disambiguationData":[TD([[makeQuery(id+"F2.imprint","IMPRINT",EDGE,{"derivedFrom":sQuery(id+"F2.wireOp",EDGE,"E28.52.0")}),1.0]])]});
            var Q5;
            Q5=makeQuery(id+"F2.imprint","IMPRINT",FACE,{"disambiguationData":[TD([[makeQuery(id+"F2.imprint","IMPRINT",EDGE,{"derivedFrom":sQuery(id+"F2.wireOp",EDGE,"E28.51.0")}),1.0]])]});
            var Q6;
            Q6=makeQuery(id+"F2.imprint","IMPRINT",FACE,{"disambiguationData":[TD([[makeQuery(id+"F2.imprint","IMPRINT",EDGE,{"derivedFrom":sQuery(id+"F2.wireOp",EDGE,"E28.50.0")}),1.0]])]});
            var Q7;
            Q7=makeQuery(id+"F2.imprint","IMPRINT",FACE,{"disambiguationData":[TD([[makeQuery(id+"F2.imprint","IMPRINT",EDGE,{"derivedFrom":sQuery(id+"F2.wireOp",EDGE,"E28.49.0")}),1.0]])]});
            var Q8;
            Q8=makeQuery(id+"F2.imprint","IMPRINT",FACE,{"disambiguationData":[TD([[makeQuery(id+"F2.imprint","IMPRINT",EDGE,{"derivedFrom":sQuery(id+"F2.wireOp",EDGE,"E28.48.0")}),1.0]])]});
            var Q9;
            Q9=makeQuery(id+"F2.imprint","IMPRINT",FACE,{"disambiguationData":[TD([[makeQuery(id+"F2.imprint","IMPRINT",EDGE,{"derivedFrom":sQuery(id+"F2.wireOp",EDGE,"E28.47.0")}),1.0]])]});
            var Q10;
            Q10=makeQuery(id+"F2.imprint","IMPRINT",FACE,{"disambiguationData":[TD([[makeQuery(id+"F2.imprint","IMPRINT",EDGE,{"derivedFrom":sQuery(id+"F2.wireOp",EDGE,"E28.46.0")}),1.0]])]});
            var Q11;
            Q11=makeQuery(id+"F2.imprint","IMPRINT",FACE,{"disambiguationData":[TD([[makeQuery(id+"F2.imprint","IMPRINT",EDGE,{"derivedFrom":sQuery(id+"F2.wireOp",EDGE,"E28.45.0")}),1.0]])]});
            var Q12;
            Q12=makeQuery(id+"F2.imprint","IMPRINT",FACE,{"disambiguationData":[TD([[makeQuery(id+"F2.imprint","IMPRINT",EDGE,{"derivedFrom":sQuery(id+"F2.wireOp",EDGE,"E28.44.0")}),1.0]])]});
            var Q13;
            Q13=makeQuery(id+"F2.imprint","IMPRINT",FACE,{"disambiguationData":[TD([[makeQuery(id+"F2.imprint","IMPRINT",EDGE,{"derivedFrom":sQuery(id+"F2.wireOp",EDGE,"E28.43.0")}),1.0]])]});
            var Q14;
            Q14=makeQuery(id+"F2.imprint","IMPRINT",FACE,{"disambiguationData":[TD([[makeQuery(id+"F2.imprint","IMPRINT",EDGE,{"derivedFrom":sQuery(id+"F2.wireOp",EDGE,"E28.42.0")}),1.0]])]});
            var Q15;
            Q15=makeQuery(id+"F2.imprint","IMPRINT",FACE,{"disambiguationData":[TD([[makeQuery(id+"F2.imprint","IMPRINT",EDGE,{"derivedFrom":sQuery(id+"F2.wireOp",EDGE,"E28.40.0")}),1.0]])]});
            var Q16;
            Q16=makeQuery(id+"F2.imprint","IMPRINT",FACE,{"disambiguationData":[TD([[makeQuery(id+"F2.imprint","IMPRINT",EDGE,{"derivedFrom":sQuery(id+"F2.wireOp",EDGE,"E28.39.0")}),1.0]])]});
            var Q17;
            Q17=makeQuery(id+"F2.imprint","IMPRINT",FACE,{"disambiguationData":[TD([[makeQuery(id+"F2.imprint","IMPRINT",EDGE,{"derivedFrom":sQuery(id+"F2.wireOp",EDGE,"E28.38.0")}),1.0]])]});
            var Q18;
            Q18=makeQuery(id+"F2.imprint","IMPRINT",FACE,{"disambiguationData":[TD([[makeQuery(id+"F2.imprint","IMPRINT",EDGE,{"derivedFrom":sQuery(id+"F2.wireOp",EDGE,"E28.37.0")}),1.0]])]});
            var Q19;
            Q19=makeQuery(id+"F2.imprint","IMPRINT",FACE,{"disambiguationData":[TD([[makeQuery(id+"F2.imprint","IMPRINT",EDGE,{"derivedFrom":sQuery(id+"F2.wireOp",EDGE,"E28.36.0")}),1.0]])]});
            var Q20;
            Q20=makeQuery(id+"F2.imprint","IMPRINT",FACE,{"disambiguationData":[TD([[makeQuery(id+"F2.imprint","IMPRINT",EDGE,{"derivedFrom":sQuery(id+"F2.wireOp",EDGE,"E28.35.0")}),1.0]])]});
            var Q21;
            Q21=makeQuery(id+"F2.imprint","IMPRINT",FACE,{"disambiguationData":[TD([[makeQuery(id+"F2.imprint","IMPRINT",EDGE,{"derivedFrom":sQuery(id+"F2.wireOp",EDGE,"E28.57.0")}),1.0]])]});
            var Q22;
            Q22=makeQuery(id+"F2.imprint","IMPRINT",FACE,{"disambiguationData":[TD([[makeQuery(id+"F2.imprint","IMPRINT",EDGE,{"derivedFrom":sQuery(id+"F2.wireOp",EDGE,"E28.58.0")}),1.0]])]});
            var Q23;
            {var subQ3=sQuery(id+"F2.wireOp",EDGE,"E17");Q23=makeQuery(id+"F2.imprint","IMPRINT",FACE,{"disambiguationData":[TD([[makeQuery(id+"F2.imprint","IMPRINT",EDGE,{"derivedFrom":subQ3}),-1.0]])]});}
            var Q24;
            Q24=makeQuery(id+"F2.imprint","IMPRINT",FACE,{"disambiguationData":[TD([[makeQuery(id+"F2.imprint","IMPRINT",EDGE,{"derivedFrom":sQuery(id+"F2.wireOp",EDGE,"E28.1.0")}),1.0]])]});
            var Q25;
            {var subQ5=sQuery(id+"F2.wireOp",EDGE,"E17");Q25=makeQuery(id+"F2.imprint","IMPRINT",FACE,{"disambiguationData":[TD([[makeQuery(id+"F2.imprint","IMPRINT",EDGE,{"derivedFrom":subQ5}),1.0]])]});}
            var Q26;
            Q26=makeQuery(id+"F2.imprint","IMPRINT",FACE,{"disambiguationData":[TD([[makeQuery(id+"F2.imprint","IMPRINT",EDGE,{"derivedFrom":sQuery(id+"F2.wireOp",EDGE,"E28.3.0")}),1.0]])]});
            var Q27;
            Q27=makeQuery(id+"F2.imprint","IMPRINT",FACE,{"disambiguationData":[TD([[makeQuery(id+"F2.imprint","IMPRINT",EDGE,{"derivedFrom":sQuery(id+"F2.wireOp",EDGE,"E28.5.0")}),1.0]])]});
            var Q28;
            Q28=makeQuery(id+"F2.imprint","IMPRINT",FACE,{"disambiguationData":[TD([[makeQuery(id+"F2.imprint","IMPRINT",EDGE,{"derivedFrom":sQuery(id+"F2.wireOp",EDGE,"E28.6.0")}),1.0]])]});
            var Q29;
            Q29=makeQuery(id+"F2.imprint","IMPRINT",FACE,{"disambiguationData":[TD([[makeQuery(id+"F2.imprint","IMPRINT",EDGE,{"derivedFrom":sQuery(id+"F2.wireOp",EDGE,"E28.7.0")}),1.0]])]});
            var Q30;
            Q30=makeQuery(id+"F2.imprint","IMPRINT",FACE,{"disambiguationData":[TD([[makeQuery(id+"F2.imprint","IMPRINT",EDGE,{"derivedFrom":sQuery(id+"F2.wireOp",EDGE,"E28.8.0")}),1.0]])]});
            var Q31;
            Q31=makeQuery(id+"F2.imprint","IMPRINT",FACE,{"disambiguationData":[TD([[makeQuery(id+"F2.imprint","IMPRINT",EDGE,{"derivedFrom":sQuery(id+"F2.wireOp",EDGE,"E28.9.0")}),1.0]])]});
            var Q32;
            Q32=makeQuery(id+"F2.imprint","IMPRINT",FACE,{"disambiguationData":[TD([[makeQuery(id+"F2.imprint","IMPRINT",EDGE,{"derivedFrom":sQuery(id+"F2.wireOp",EDGE,"E28.10.0")}),1.0]])]});
            var Q33;
            Q33=makeQuery(id+"F2.imprint","IMPRINT",FACE,{"disambiguationData":[TD([[makeQuery(id+"F2.imprint","IMPRINT",EDGE,{"derivedFrom":sQuery(id+"F2.wireOp",EDGE,"E28.11.0")}),1.0]])]});
            var Q34;
            Q34=makeQuery(id+"F2.imprint","IMPRINT",FACE,{"disambiguationData":[TD([[makeQuery(id+"F2.imprint","IMPRINT",EDGE,{"derivedFrom":sQuery(id+"F2.wireOp",EDGE,"E28.12.0")}),1.0]])]});
            var Q35;
            Q35=makeQuery(id+"F2.imprint","IMPRINT",FACE,{"disambiguationData":[TD([[makeQuery(id+"F2.imprint","IMPRINT",EDGE,{"derivedFrom":sQuery(id+"F2.wireOp",EDGE,"E28.13.0")}),1.0]])]});
            var Q36;
            Q36=makeQuery(id+"F2.imprint","IMPRINT",FACE,{"disambiguationData":[TD([[makeQuery(id+"F2.imprint","IMPRINT",EDGE,{"derivedFrom":sQuery(id+"F2.wireOp",EDGE,"E28.14.0")}),1.0]])]});
            var Q37;
            Q37=makeQuery(id+"F2.imprint","IMPRINT",FACE,{"disambiguationData":[TD([[makeQuery(id+"F2.imprint","IMPRINT",EDGE,{"derivedFrom":sQuery(id+"F2.wireOp",EDGE,"E28.15.0")}),1.0]])]});
            var Q38;
            Q38=makeQuery(id+"F2.imprint","IMPRINT",FACE,{"disambiguationData":[TD([[makeQuery(id+"F2.imprint","IMPRINT",EDGE,{"derivedFrom":sQuery(id+"F2.wireOp",EDGE,"E28.16.0")}),1.0]])]});
            var Q39;
            Q39=makeQuery(id+"F2.imprint","IMPRINT",FACE,{"disambiguationData":[TD([[makeQuery(id+"F2.imprint","IMPRINT",EDGE,{"derivedFrom":sQuery(id+"F2.wireOp",EDGE,"E28.17.0")}),1.0]])]});
            var Q40;
            Q40=makeQuery(id+"F2.imprint","IMPRINT",FACE,{"disambiguationData":[TD([[makeQuery(id+"F2.imprint","IMPRINT",EDGE,{"derivedFrom":sQuery(id+"F2.wireOp",EDGE,"E28.18.0")}),1.0]])]});
            var Q41;
            Q41=makeQuery(id+"F2.imprint","IMPRINT",FACE,{"disambiguationData":[TD([[makeQuery(id+"F2.imprint","IMPRINT",EDGE,{"derivedFrom":sQuery(id+"F2.wireOp",EDGE,"E28.19.0")}),1.0]])]});
            var Q42;
            Q42=makeQuery(id+"F2.imprint","IMPRINT",FACE,{"disambiguationData":[TD([[makeQuery(id+"F2.imprint","IMPRINT",EDGE,{"derivedFrom":sQuery(id+"F2.wireOp",EDGE,"E28.20.0")}),1.0]])]});
            var Q43;
            Q43=makeQuery(id+"F2.imprint","IMPRINT",FACE,{"disambiguationData":[TD([[makeQuery(id+"F2.imprint","IMPRINT",EDGE,{"derivedFrom":sQuery(id+"F2.wireOp",EDGE,"E28.21.0")}),1.0]])]});
            var Q44;
            Q44=makeQuery(id+"F2.imprint","IMPRINT",FACE,{"disambiguationData":[TD([[makeQuery(id+"F2.imprint","IMPRINT",EDGE,{"derivedFrom":sQuery(id+"F2.wireOp",EDGE,"E28.22.0")}),1.0]])]});
            var Q45;
            Q45=makeQuery(id+"F2.imprint","IMPRINT",FACE,{"disambiguationData":[TD([[makeQuery(id+"F2.imprint","IMPRINT",EDGE,{"derivedFrom":sQuery(id+"F2.wireOp",EDGE,"E28.23.0")}),1.0]])]});
            var Q46;
            Q46=makeQuery(id+"F2.imprint","IMPRINT",FACE,{"disambiguationData":[TD([[makeQuery(id+"F2.imprint","IMPRINT",EDGE,{"derivedFrom":sQuery(id+"F2.wireOp",EDGE,"E28.24.0")}),1.0]])]});
            var Q47;
            Q47=makeQuery(id+"F2.imprint","IMPRINT",FACE,{"disambiguationData":[TD([[makeQuery(id+"F2.imprint","IMPRINT",EDGE,{"derivedFrom":sQuery(id+"F2.wireOp",EDGE,"E28.25.0")}),1.0]])]});
            var Q48;
            Q48=makeQuery(id+"F2.imprint","IMPRINT",FACE,{"disambiguationData":[TD([[makeQuery(id+"F2.imprint","IMPRINT",EDGE,{"derivedFrom":sQuery(id+"F2.wireOp",EDGE,"E28.26.0")}),1.0]])]});
            var Q49;
            Q49=makeQuery(id+"F2.imprint","IMPRINT",FACE,{"disambiguationData":[TD([[makeQuery(id+"F2.imprint","IMPRINT",EDGE,{"derivedFrom":sQuery(id+"F2.wireOp",EDGE,"E28.27.0")}),1.0]])]});
            var Q50;
            Q50=makeQuery(id+"F2.imprint","IMPRINT",FACE,{"disambiguationData":[TD([[makeQuery(id+"F2.imprint","IMPRINT",EDGE,{"derivedFrom":sQuery(id+"F2.wireOp",EDGE,"E28.28.0")}),1.0]])]});
            var Q51;
            Q51=makeQuery(id+"F2.imprint","IMPRINT",FACE,{"disambiguationData":[TD([[makeQuery(id+"F2.imprint","IMPRINT",EDGE,{"derivedFrom":sQuery(id+"F2.wireOp",EDGE,"E28.29.0")}),1.0]])]});
            var Q52;
            Q52=makeQuery(id+"F2.imprint","IMPRINT",FACE,{"disambiguationData":[TD([[makeQuery(id+"F2.imprint","IMPRINT",EDGE,{"derivedFrom":sQuery(id+"F2.wireOp",EDGE,"E28.31.0")}),1.0]])]});
            var Q53;
            Q53=makeQuery(id+"F2.imprint","IMPRINT",FACE,{"disambiguationData":[TD([[makeQuery(id+"F2.imprint","IMPRINT",EDGE,{"derivedFrom":sQuery(id+"F2.wireOp",EDGE,"E28.32.0")}),1.0]])]});
            var Q54;
            Q54=makeQuery(id+"F2.imprint","IMPRINT",FACE,{"disambiguationData":[TD([[makeQuery(id+"F2.imprint","IMPRINT",EDGE,{"derivedFrom":sQuery(id+"F2.wireOp",EDGE,"E28.33.0")}),1.0]])]});
            var Q55;
            Q55=makeQuery(id+"F2.imprint","IMPRINT",FACE,{"disambiguationData":[TD([[makeQuery(id+"F2.imprint","IMPRINT",EDGE,{"derivedFrom":sQuery(id+"F2.wireOp",EDGE,"E28.34.0")}),1.0]])]});
            var Q56;
            Q56=makeQuery(id+"F2.imprint","IMPRINT",FACE,{"disambiguationData":[TD([[makeQuery(id+"F2.imprint","IMPRINT",EDGE,{"derivedFrom":sQuery(id+"F2.wireOp",EDGE,"E28.4.0")}),1.0]])]});
            var Q57;
            Q57=makeQuery(id+"F2.imprint","IMPRINT",FACE,{"disambiguationData":[TD([[makeQuery(id+"F2.imprint","IMPRINT",EDGE,{"derivedFrom":sQuery(id+"F2.wireOp",EDGE,"E28.30.0")}),1.0]])]});
            var Q58;
            Q58=makeQuery(id+"F2.imprint","IMPRINT",FACE,{"disambiguationData":[TD([[makeQuery(id+"F2.imprint","IMPRINT",EDGE,{"derivedFrom":sQuery(id+"F2.wireOp",EDGE,"E28.2.0")}),1.0]])]});
            var Q59;
            Q59=makeQuery(id+"F2.imprint","IMPRINT",FACE,{"disambiguationData":[TD([[makeQuery(id+"F2.imprint","IMPRINT",EDGE,{"derivedFrom":sQuery(id+"F2.wireOp",EDGE,"E28.41.0")}),1.0]])]});
            extrude(context, id + "F3", {"entities" : qUnion([Q0, Q1, Q2, Q3, Q4, Q5, Q6, Q7, Q8, Q9, Q10, Q11, Q12, Q13, Q14, Q15, Q16, Q17, Q18, Q19, Q20, Q21, Q22, Q23, Q24, Q25, Q26, Q27, Q28, Q29, Q30, Q31, Q32, Q33, Q34, Q35, Q36, Q37, Q38, Q39, Q40, Q41, Q42, Q43, Q44, Q45, Q46, Q47, Q48, Q49, Q50, Q51, Q52, Q53, Q54, Q55, Q56, Q57, Q58, Q59]), "operationType" : NewBodyOperationType.ADD, "depth" : 12.1 * mm, "offsetDistance" : 25 * mm});
        }
        {
            var Q0;
            Q0=makeQuery(id+"F1.opRevolve","SWEPT_FACE",FACE,{"disambiguationData":[OSD([sQuery(id+"F0.wireOp",EDGE,"E14")])]});
            var sketch = newSketch(context, id + "F4", { "sketchPlane" : qUnion([Q0])});
            skCircle(sketch, "E29", {"center": v(0, 0) * mm, "radius": 11.9 * mm});
            skCircle(sketch, "E30", {"center": v(0, 0) * mm, "radius": 5.5 * mm});
            skLineSegment(sketch, "E31", {"start": v(-1.75, 11.77) * mm, "end": v(-2.01, 5.92) * mm});
            skArc(sketch, "E32", {"start": v(-2.7, 4.79) * mm, "mid": v(-2.21, 5.26) * mm, "end": v(-2.01, 5.92) * mm});
            skPoint(sketch, "E32.first.point", {"position": v(-2.7, 4.79) * mm});
            skPoint(sketch, "E32.second.point", {"position": v(-2.01, 5.92) * mm});
            skPoint(sketch, "E33.orphan", {"position": v(-2.05, 5.1) * mm});
            skLineSegment(sketch, "E34.MirrorCS", {"start": v(1.75, 11.77) * mm, "end": v(2.01, 5.92) * mm});
            skArc(sketch, "E35.MirrorCS", {"start": v(2.7, 4.79) * mm, "mid": v(2.21, 5.26) * mm, "end": v(2.01, 5.92) * mm});
            skLineSegment(sketch, "E36.1.0", {"start": v(-11.74, 1.97) * mm, "end": v(-6.25, -0.09) * mm});
            skLineSegment(sketch, "E36.1.1", {"start": v(-10.65, 5.3) * mm, "end": v(-5, 3.74) * mm});
            skArc(sketch, "E36.1.2", {"start": v(-3.72, 4.05) * mm, "mid": v(-4.32, 3.73) * mm, "end": v(-5, 3.74) * mm});
            skArc(sketch, "E36.1.3", {"start": v(-5.39, -1.1) * mm, "mid": v(-5.69, -0.48) * mm, "end": v(-6.25, -0.09) * mm});
            skLineSegment(sketch, "E36.2.0", {"start": v(-5.5, -10.55) * mm, "end": v(-1.85, -5.97) * mm});
            skLineSegment(sketch, "E36.2.1", {"start": v(-8.33, -8.5) * mm, "end": v(-5.1, -3.6) * mm});
            skArc(sketch, "E36.2.2", {"start": v(-5, -2.28) * mm, "mid": v(-4.89, -2.96) * mm, "end": v(-5.1, -3.6) * mm});
            skArc(sketch, "E36.2.3", {"start": v(-0.62, -5.46) * mm, "mid": v(-1.3, -5.56) * mm, "end": v(-1.85, -5.97) * mm});
            skLineSegment(sketch, "E36.3.0", {"start": v(8.33, -8.5) * mm, "end": v(5.1, -3.6) * mm});
            skLineSegment(sketch, "E36.3.1", {"start": v(5.5, -10.55) * mm, "end": v(1.85, -5.97) * mm});
            skArc(sketch, "E36.3.2", {"start": v(0.62, -5.46) * mm, "mid": v(1.3, -5.56) * mm, "end": v(1.85, -5.97) * mm});
            skArc(sketch, "E36.3.3", {"start": v(5, -2.28) * mm, "mid": v(4.89, -2.96) * mm, "end": v(5.1, -3.6) * mm});
            skLineSegment(sketch, "E36.4.0", {"start": v(10.65, 5.3) * mm, "end": v(5, 3.74) * mm});
            skLineSegment(sketch, "E36.4.1", {"start": v(11.74, 1.97) * mm, "end": v(6.25, -0.09) * mm});
            skArc(sketch, "E36.4.2", {"start": v(5.39, -1.1) * mm, "mid": v(5.69, -0.48) * mm, "end": v(6.25, -0.09) * mm});
            skArc(sketch, "E36.4.3", {"start": v(3.72, 4.05) * mm, "mid": v(4.32, 3.73) * mm, "end": v(5, 3.74) * mm});
            skSolve(sketch);
        }
        {
            var Q0;
            {var subQ0=sQuery(id+"F4.wireOp",EDGE,"E31");var subQ1=sQuery(id+"F4.wireOp",EDGE,"E29");var subQ2=makeQuery(id+"F4.imprint","INTERSECT",VERTEX,{"derivedFrom":[subQ1,subQ0]});Q0=makeQuery(id+"F4.imprint","IMPRINT",FACE,{"disambiguationData":[TD([[makeQuery(id+"F4.imprint","IMPRINT",EDGE,{"disambiguationData":[TD([[subQ2,1.0]])],"derivedFrom":subQ1}),1.0]])]});}
            var Q1;
            {var subQ4=sQuery(id+"F4.wireOp",EDGE,"E32");Q1=makeQuery(id+"F4.imprint","IMPRINT",FACE,{"disambiguationData":[TD([[makeQuery(id+"F4.imprint","IMPRINT",EDGE,{"derivedFrom":subQ4}),-1.0]])]});}
            var Q2;
            {var subQ0=sQuery(id+"F4.wireOp",EDGE,"E36.1.0");var subQ1=sQuery(id+"F4.wireOp",EDGE,"E29");var subQ2=makeQuery(id+"F4.imprint","INTERSECT",VERTEX,{"derivedFrom":[subQ1,subQ0]});Q2=makeQuery(id+"F4.imprint","IMPRINT",FACE,{"disambiguationData":[TD([[makeQuery(id+"F4.imprint","IMPRINT",EDGE,{"disambiguationData":[TD([[subQ2,1.0]])],"derivedFrom":subQ1}),1.0]])]});}
            var Q3;
            {var subQ0=sQuery(id+"F4.wireOp",EDGE,"E36.1.2");Q3=makeQuery(id+"F4.imprint","IMPRINT",FACE,{"disambiguationData":[TD([[makeQuery(id+"F4.imprint","IMPRINT",EDGE,{"derivedFrom":subQ0}),1.0]])]});}
            var Q4;
            {var subQ0=sQuery(id+"F4.wireOp",EDGE,"E36.4.0");var subQ1=sQuery(id+"F4.wireOp",EDGE,"E29");var subQ2=makeQuery(id+"F4.imprint","INTERSECT",VERTEX,{"derivedFrom":[subQ1,subQ0]});Q4=makeQuery(id+"F4.imprint","IMPRINT",FACE,{"disambiguationData":[TD([[makeQuery(id+"F4.imprint","IMPRINT",EDGE,{"disambiguationData":[TD([[subQ2,1.0]])],"derivedFrom":subQ1}),1.0]])]});}
            var Q5;
            {var subQ0=sQuery(id+"F4.wireOp",EDGE,"E36.4.2");Q5=makeQuery(id+"F4.imprint","IMPRINT",FACE,{"disambiguationData":[TD([[makeQuery(id+"F4.imprint","IMPRINT",EDGE,{"derivedFrom":subQ0}),1.0]])]});}
            var Q6;
            {var subQ0=sQuery(id+"F4.wireOp",EDGE,"E30");var subQ4=makeQuery(id+"F4.imprint","INTERSECT",VERTEX,{"derivedFrom":[subQ0,sQuery(id+"F4.wireOp",EDGE,"E35.MirrorCS")]});Q6=makeQuery(id+"F4.imprint","IMPRINT",FACE,{"disambiguationData":[TD([[makeQuery(id+"F4.imprint","IMPRINT",EDGE,{"disambiguationData":[TD([[subQ4,1.0]])],"derivedFrom":subQ0}),1.0]])]});}
            var Q7;
            {var subQ0=sQuery(id+"F4.wireOp",EDGE,"E36.2.2");Q7=makeQuery(id+"F4.imprint","IMPRINT",FACE,{"disambiguationData":[TD([[makeQuery(id+"F4.imprint","IMPRINT",EDGE,{"derivedFrom":subQ0}),1.0]])]});}
            var Q8;
            {var subQ0=sQuery(id+"F4.wireOp",EDGE,"E36.3.2");Q8=makeQuery(id+"F4.imprint","IMPRINT",FACE,{"disambiguationData":[TD([[makeQuery(id+"F4.imprint","IMPRINT",EDGE,{"derivedFrom":subQ0}),1.0]])]});}
            var Q9;
            {var subQ0=sQuery(id+"F4.wireOp",EDGE,"E36.2.0");var subQ1=sQuery(id+"F4.wireOp",EDGE,"E29");var subQ2=makeQuery(id+"F4.imprint","INTERSECT",VERTEX,{"derivedFrom":[subQ1,subQ0]});Q9=makeQuery(id+"F4.imprint","IMPRINT",FACE,{"disambiguationData":[TD([[makeQuery(id+"F4.imprint","IMPRINT",EDGE,{"disambiguationData":[TD([[subQ2,1.0]])],"derivedFrom":subQ1}),1.0]])]});}
            var Q10;
            {var subQ0=sQuery(id+"F4.wireOp",EDGE,"E36.3.0");var subQ1=sQuery(id+"F4.wireOp",EDGE,"E29");var subQ2=makeQuery(id+"F4.imprint","INTERSECT",VERTEX,{"derivedFrom":[subQ1,subQ0]});Q10=makeQuery(id+"F4.imprint","IMPRINT",FACE,{"disambiguationData":[TD([[makeQuery(id+"F4.imprint","IMPRINT",EDGE,{"disambiguationData":[TD([[subQ2,1.0]])],"derivedFrom":subQ1}),1.0]])]});}
            extrude(context, id + "F5", {"entities" : qUnion([Q0, Q1, Q2, Q3, Q4, Q5, Q6, Q7, Q8, Q9, Q10]), "endBound" : BoundingType.SYMMETRIC, "depth" : 25 * mm, "offsetDistance" : 25 * mm});
        }
        {
            var Q0;
            Q0=makeQuery(id+"F5.opExtrude","SWEPT_BODY",BODY,{"disambiguationData":[OSD([sQuery(id+"F4.wireOp",EDGE,"E29"),sQuery(id+"F4.wireOp",EDGE,"E30"),sQuery(id+"F4.wireOp",EDGE,"E31"),sQuery(id+"F4.wireOp",EDGE,"E32"),sQuery(id+"F4.wireOp",EDGE,"E34.MirrorCS"),sQuery(id+"F4.wireOp",EDGE,"E35.MirrorCS"),sQuery(id+"F4.wireOp",EDGE,"E36.1.0"),sQuery(id+"F4.wireOp",EDGE,"E36.1.1"),sQuery(id+"F4.wireOp",EDGE,"E36.1.2"),sQuery(id+"F4.wireOp",EDGE,"E36.1.3"),sQuery(id+"F4.wireOp",EDGE,"E36.2.0"),sQuery(id+"F4.wireOp",EDGE,"E36.2.1"),sQuery(id+"F4.wireOp",EDGE,"E36.2.2"),sQuery(id+"F4.wireOp",EDGE,"E36.2.3"),sQuery(id+"F4.wireOp",EDGE,"E36.3.0"),sQuery(id+"F4.wireOp",EDGE,"E36.3.1"),sQuery(id+"F4.wireOp",EDGE,"E36.3.2"),sQuery(id+"F4.wireOp",EDGE,"E36.3.3"),sQuery(id+"F4.wireOp",EDGE,"E36.4.0"),sQuery(id+"F4.wireOp",EDGE,"E36.4.1"),sQuery(id+"F4.wireOp",EDGE,"E36.4.2"),sQuery(id+"F4.wireOp",EDGE,"E36.4.3")])]});
            var Q1;
            Q1=makeQuery(id+"F1.opRevolve","SWEPT_BODY",BODY,{"disambiguationData":[OSD([sQuery(id+"F0.wireOp",EDGE,"E0"),sQuery(id+"F0.wireOp",EDGE,"E1"),sQuery(id+"F0.wireOp",EDGE,"E2"),sQuery(id+"F0.wireOp",EDGE,"E3"),sQuery(id+"F0.wireOp",EDGE,"E4"),sQuery(id+"F0.wireOp",EDGE,"E5"),sQuery(id+"F0.wireOp",EDGE,"E6"),sQuery(id+"F0.wireOp",EDGE,"E7"),sQuery(id+"F0.wireOp",EDGE,"E8"),sQuery(id+"F0.wireOp",EDGE,"E9"),sQuery(id+"F0.wireOp",EDGE,"E10"),sQuery(id+"F0.wireOp",EDGE,"E11"),sQuery(id+"F0.wireOp",EDGE,"E12"),sQuery(id+"F0.wireOp",EDGE,"E13"),sQuery(id+"F0.wireOp",EDGE,"E14"),sQuery(id+"F0.wireOp",EDGE,"E15")])]});
            booleanBodies(context, id + "F6", {"operationType" : BooleanOperationType.SUBTRACTION, "tools" : qUnion([Q0]), "targets" : qUnion([Q1])});
        }
    });
